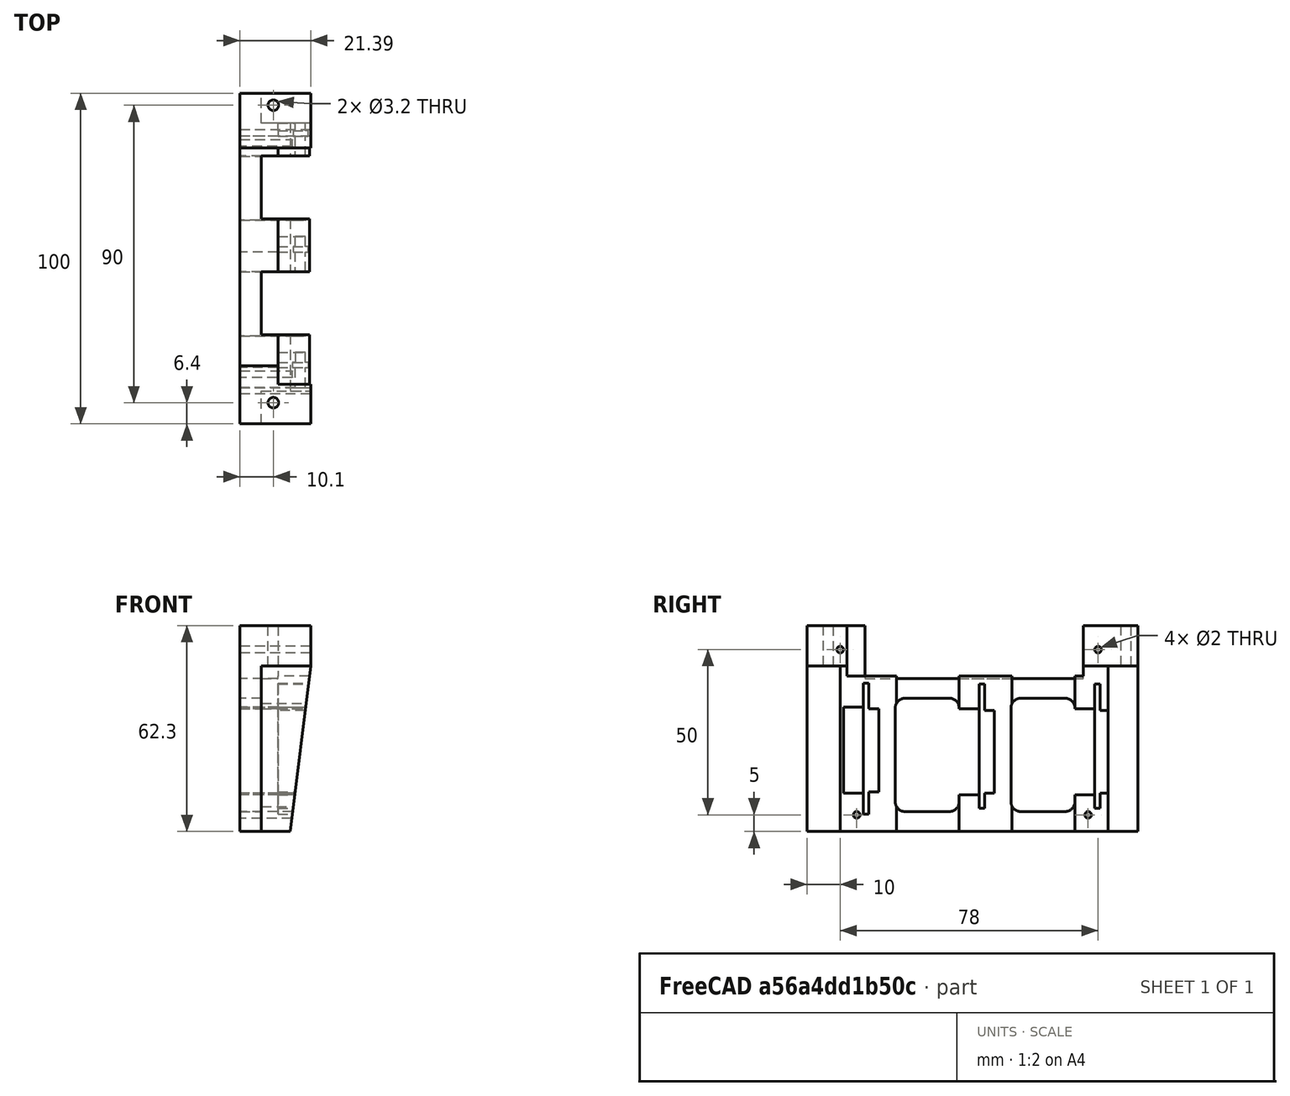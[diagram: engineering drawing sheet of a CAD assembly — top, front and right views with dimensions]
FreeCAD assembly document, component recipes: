
FREECAD ASSEMBLY — COMPONENT RECIPES ("sborka")

This assembly document has 10 components, labeled P0..P9 below (a component is one placed body or linked part). 7 of them carry a construction recipe — the FreeCAD feature program that regenerates the part from scratch, quoted from this document or its linked companion documents; the rest are supplied as boundary geometry only. No exploded tour is included for this assembly.
COMPONENT P0 — geometry summary ("keypad"; no construction recipe available for this part):
  bounding box: 75.0 x 69.0 x 2.0 mm
  tessellated surface: 12 triangles
  volume: 10350 mm^3 (100% of its bounding box)
  symmetry: 2-fold rotationally symmetric about the x axis; 2-fold rotationally symmetric about the y axis; 2-fold rotationally symmetric about the z axis; mirror-symmetric across its x mid-plane, z mid-plane
COMPONENT P1 — geometry summary ("3_97inch_LCD001"; no construction recipe available for this part):
  bounding box: 112.0 x 59.5 x 14.1 mm
  tessellated surface: 92 triangles
  volume: 35557 mm^3 (38% of its bounding box)
  symmetry: mirror-symmetric across its z mid-plane
COMPONENT P2 — recipe-attached ("acd_dac_board", a linked part whose construction recipe lives in a companion FreeCAD document of the same project; that document's serialized recipe follows).
Construction recipe (the companion document, serialized — sketch geometry with constraints, then the solid features built on it; lengths are millimeters unless a unit is written):

FCSTD DOCUMENT  (FreeCAD 1.0R39109 (Git))
Label: acd_dac_board
License: All rights reserved
LicenseURL: https://en.wikipedia.org/wiki/All_rights_reserved
objects: App::Part×6, App::Link×5, Part::Feature×4, PartDesign::CoordinateSystem×1, Sketcher::SketchObject×1
note: 7 computed .brp shape members not serialized (recipe doc carries the construction recipe); baked Part::Feature solids carry a one-line shape summary decoded from their .brp

FEATURE [PartDesign::CoordinateSystem] Local_CS_c5fe
  AttacherType = Attacher::AttachEngine3D
  MapMode = 2
FEATURE [Part::Feature] Pcb_c5fe
  shape: bbox 90 x 60 x 1.6 mm, 120 faces (baked)
FEATURE [Sketcher::SketchObject] PCB_Sketch_c5fe
  ArcFitTolerance = 1e-06
  FullyConstrained = false
  MakeInternals = false
  sketch-geometry (4):
    g0: LineSegment StartX=93.9 StartY=-71.9 StartZ=0 EndX=183.9 EndY=-71.9 EndZ=0
    g1: LineSegment StartX=183.9 StartY=-71.9 StartZ=0 EndX=183.9 EndY=-131.9 EndZ=0
    g2: LineSegment StartX=183.9 StartY=-131.9 StartZ=0 EndX=93.9 EndY=-131.9 EndZ=0
    g3: LineSegment StartX=93.9 StartY=-131.9 StartZ=0 EndX=93.9 EndY=-71.9 EndZ=0
  constraints (4):
    c: Coincident(g2,g3)
    c: Coincident(g0,g3)
    c: Coincident(g1,g2)
    c: Coincident(g0,g1)
FEATURE [App::Part] Board_Geoms_c5fe
  Group = -> [Pcb_c5fe,PCB_Sketch_c5fe]
  Origin = -> Origin
FEATURE [Part::Feature] Shape  label="J4_PinHeader_2x25_P254mm_Horizontal_27a54bd5aef3"
  Placement = pos=(168.5,-117.06,0) rot=(0,0,-1;1.5708rad)
  shape: bbox 63.5 x 12.9 x 8.08 mm, 1204 faces (baked)
FEATURE [Part::Feature] Shape001  label="J3_PinSocket_2x10_P2.54mm_Vertical_5a6bbbb15814"
  Placement = pos=(174.8,-83.06,0) rot=(0,0,1;0rad)
  shape: bbox 5.08 x 25.4 x 11.6 mm, 530 faces (baked)
FEATURE [App::Link] J3_PinSocket_2x10_P2_54mm_Vertical_5a6bbbb15814_ln_  label="J1_PinSocket_2x10_P2.54mm_Vertical_580dcfef748e"
  LinkPlacement = pos=(104.8,-83.06,0) rot=(0,0,1;0rad)
  LinkedObject = -> Shape001
  Placement = pos=(104.8,-83.06,0) rot=(0,0,1;0rad)
FEATURE [App::Link] J3_PinSocket_2x10_P2_54mm_Vertical_5a6bbbb15814_ln_001  label="J2_PinSocket_2x10_P2.54mm_Vertical_61ef51b03cdf"
  LinkPlacement = pos=(139.8,-83.06,0) rot=(0,0,1;0rad)
  LinkedObject = -> Shape001
  Placement = pos=(139.8,-83.06,0) rot=(0,0,1;0rad)
FEATURE [App::Part] Top_c5fe
  Group = -> [Shape,Shape001,J3_PinSocket_2x10_P2_54mm_Vertical_5a6bbbb15814_ln_,J3_PinSocket_2x10_P2_54mm_Vertical_5a6bbbb15814_ln_001]
  Origin = -> Origin003
FEATURE [App::Part] Step_Models_c5fe
  Group = -> [Top_c5fe]
  Origin = -> Origin002
FEATURE [Part::Feature] Shape002  label="REF_2.5 mmx7-Screw_fc498af58895"
  Placement = pos=(173,-75.1,-1.6) rot=(0,1,0;3.14159rad)
  shape: bbox 5 x 5 x 8.693 mm, 8 faces (baked)
FEATURE [App::Link] REF_2_5_mmx7_Screw_fc498af58895_ln_  label="REF_REF_2.5 mmx7-Screw_7bb2b2d65ce1"
  LinkPlacement = pos=(178,-125.1,-1.6) rot=(0,1,0;3.14159rad)
  LinkedObject = -> Shape002
  Placement = pos=(178,-125.1,-1.6) rot=(0,1,0;3.14159rad)
FEATURE [App::Link] REF_2_5_mmx7_Screw_fc498af58895_ln_001  label="REF_REF_2.5 mmx7-Screw_5b3bb718906a"
  LinkPlacement = pos=(99.9,-125.1,-1.6) rot=(0,1,0;3.14159rad)
  LinkedObject = -> Shape002
  Placement = pos=(99.9,-125.1,-1.6) rot=(0,1,0;3.14159rad)
FEATURE [App::Link] REF_2_5_mmx7_Screw_fc498af58895_ln_002  label="REF_REF_2.5 mmx7-Screw_1ec84486e3c5"
  LinkPlacement = pos=(103,-75.1,-1.6) rot=(0,1,0;3.14159rad)
  LinkedObject = -> Shape002
  Placement = pos=(103,-75.1,-1.6) rot=(0,1,0;3.14159rad)
FEATURE [App::Part] BotV_c5fe
  Group = -> [Shape002,REF_2_5_mmx7_Screw_fc498af58895_ln_,REF_2_5_mmx7_Screw_fc498af58895_ln_001,REF_2_5_mmx7_Screw_fc498af58895_ln_002]
  Origin = -> Origin007
FEATURE [App::Part] Step_Virtual_Models_c5fe
  Group = -> [BotV_c5fe]
  Origin = -> Origin005
FEATURE [App::Part] Board_c5fe  label="acd_dac_board"
  Group = -> [Local_CS_c5fe,Board_Geoms_c5fe,Step_Models_c5fe,Step_Virtual_Models_c5fe]
  Origin = -> Origin001
COMPONENT P3 — recipe-attached ("adc", a linked part whose construction recipe lives in a companion FreeCAD document of the same project; that document's serialized recipe follows).
Construction recipe (the companion document, serialized — sketch geometry with constraints, then the solid features built on it; lengths are millimeters unless a unit is written):

FCSTD DOCUMENT  (FreeCAD 1.0R39109 (Git))
Label: ADC
License: All rights reserved
LicenseURL: https://en.wikipedia.org/wiki/All_rights_reserved
objects: App::Link×34, Part::Feature×13, App::Part×4, PartDesign::CoordinateSystem×1, Sketcher::SketchObject×1
note: 16 computed .brp shape members not serialized (recipe doc carries the construction recipe); baked Part::Feature solids carry a one-line shape summary decoded from their .brp

FEATURE [PartDesign::CoordinateSystem] Local_CS_3770
  AttacherType = Attacher::AttachEngine3D
  MapMode = 2
FEATURE [Part::Feature] Pcb_3770
  Placement = pos=(-93.74,138.54,0) rot=(0,0,1;0rad)
  shape: bbox 37 x 54 x 1.6 mm, 39 faces (baked)
FEATURE [Sketcher::SketchObject] PCB_Sketch_3770
  ArcFitTolerance = 1e-06
  FullyConstrained = false
  MakeInternals = false
  sketch-geometry (4):
    g0: LineSegment StartX=-31.24 StartY=51.04 StartZ=0 EndX=5.76 EndY=51.04 EndZ=0
    g1: LineSegment StartX=5.76 StartY=51.04 StartZ=0 EndX=5.76 EndY=-2.96 EndZ=0
    g2: LineSegment StartX=5.76 StartY=-2.96 StartZ=0 EndX=-31.24 EndY=-2.96 EndZ=0
    g3: LineSegment StartX=-31.24 StartY=-2.96 StartZ=0 EndX=-31.24 EndY=51.04 EndZ=0
  constraints (4):
    c: Coincident(g2,g3)
    c: Coincident(g0,g3)
    c: Coincident(g1,g2)
    c: Coincident(g0,g1)
FEATURE [App::Part] Board_Geoms_3770
  Group = -> [Pcb_3770,PCB_Sketch_3770]
  Origin = -> Origin
FEATURE [Part::Feature] Shape  label="REF_R_1206_3216Metric_301ddd0c36ed"
  Placement = pos=(-5.34,45.84,0) rot=(0,0,1;0rad)
  shape: bbox 3.2 x 1.6 x 0.55 mm, 26 faces (baked)
FEATURE [App::Link] REF_R_1206_3216Metric_301ddd0c36ed_ln_  label="REF_REF_R_1206_3216Metric_70df84f1ae34"
  LinkPlacement = pos=(-22.84,41.94,0) rot=(0,0,1;1.5708rad)
  LinkedObject = -> Shape
  Placement = pos=(-22.84,41.94,0) rot=(0,0,1;1.5708rad)
FEATURE [App::Link] REF_R_1206_3216Metric_301ddd0c36ed_ln_001  label="REF_REF_R_1206_3216Metric_a6f854153131"
  LinkPlacement = pos=(1.16,14.24,0) rot=(0,0,1;0rad)
  LinkedObject = -> Shape
  Placement = pos=(1.16,14.24,0) rot=(0,0,1;0rad)
FEATURE [Part::Feature] Shape001  label="REF_C_1206_3216Metric_e221a3b84079"
  Placement = pos=(-9.14,29.34,0) rot=(0,0,1;0rad)
  shape: bbox 3.2 x 1.6 x 1.6 mm, 28 faces (baked)
FEATURE [App::Link] REF_R_1206_3216Metric_301ddd0c36ed_ln_002  label="REF_REF_R_1206_3216Metric_a0f92e46f677"
  LinkPlacement = pos=(-10.64,32.94,0) rot=(0,0,1;1.5708rad)
  LinkedObject = -> Shape
  Placement = pos=(-10.64,32.94,0) rot=(0,0,1;1.5708rad)
FEATURE [Part::Feature] Shape002  label="REF_CP_Elec_63x77_d1b758cef271"
  Placement = pos=(-26.34,25.34,0) rot=(0,0,1;0rad)
  shape: bbox 8.606 x 8.603 x 7.7 mm, 41 faces (baked)
FEATURE [App::Link] REF_R_1206_3216Metric_301ddd0c36ed_ln_003  label="REF_REF_R_1206_3216Metric_1b9d2568f397"
  LinkPlacement = pos=(-20.24,41.94,0) rot=(0,0,1;1.5708rad)
  LinkedObject = -> Shape
  Placement = pos=(-20.24,41.94,0) rot=(0,0,1;1.5708rad)
FEATURE [Part::Feature] Shape003  label="REF_SOIC-8-1EP_3.9x4.9mm_P1.27mm_EP2.29x3mm_4b1fed1f54c1"
  Placement = pos=(-11.94,38.14,0) rot=(0,0,1;3.14159rad)
  shape: bbox 6 x 4.9 x 1.55 mm, 152 faces (baked)
FEATURE [App::Link] REF_C_1206_3216Metric_e221a3b84079_ln_  label="REF_REF_C_1206_3216Metric_3e90dc9b15e9"
  LinkPlacement = pos=(-1.24,27.14,0) rot=(0,0,1;0rad)
  LinkedObject = -> Shape001
  Placement = pos=(-1.24,27.14,0) rot=(0,0,1;0rad)
FEATURE [App::Link] REF_C_1206_3216Metric_e221a3b84079_ln_001  label="REF_REF_C_1206_3216Metric_f21636db2d26"
  LinkPlacement = pos=(-7.14,24.54,0) rot=(0,0,1;0rad)
  LinkedObject = -> Shape001
  Placement = pos=(-7.14,24.54,0) rot=(0,0,1;0rad)
FEATURE [App::Link] REF_C_1206_3216Metric_e221a3b84079_ln_002  label="REF_REF_C_1206_3216Metric_18777c7b1951"
  LinkPlacement = pos=(-10.74,25.34,0) rot=(0,0,1;1.5708rad)
  LinkedObject = -> Shape001
  Placement = pos=(-10.74,25.34,0) rot=(0,0,1;1.5708rad)
FEATURE [App::Link] REF_R_1206_3216Metric_301ddd0c36ed_ln_004  label="REF_REF_R_1206_3216Metric_5a7a546a1d58"
  LinkPlacement = pos=(0.96,22.24,0) rot=(0,0,1;0rad)
  LinkedObject = -> Shape
  Placement = pos=(0.96,22.24,0) rot=(0,0,1;0rad)
FEATURE [App::Link] REF_R_1206_3216Metric_301ddd0c36ed_ln_005  label="REF_REF_R_1206_3216Metric_6cf90c486473"
  LinkPlacement = pos=(-18.04,8.54,0) rot=(0,0,1;1.5708rad)
  LinkedObject = -> Shape
  Placement = pos=(-18.04,8.54,0) rot=(0,0,1;1.5708rad)
FEATURE [Part::Feature] Shape004  label="REF_LED_1206_3216Metric_2fccf6a8874c"
  Placement = pos=(-21.24,30.24,0) rot=(0,0,1;1.5708rad)
  shape: bbox 1.6 x 3.2 x 1.1 mm, 50 faces (baked)
FEATURE [Part::Feature] Shape005  label="REF_PinHeader_1x02_P254mm_Vertical_da5b8ef0d3b1"
  Placement = pos=(-22.24,49.24,0) rot=(0,0,1;1.5708rad)
  shape: bbox 5.08 x 2.54 x 11.54 mm, 52 faces (baked)
FEATURE [App::Link] REF_C_1206_3216Metric_e221a3b84079_ln_003  label="REF_REF_C_1206_3216Metric_64c44e93813f"
  LinkPlacement = pos=(-16.44,19.84,0) rot=(0,0,1;1.5708rad)
  LinkedObject = -> Shape001
  Placement = pos=(-16.44,19.84,0) rot=(0,0,1;1.5708rad)
FEATURE [App::Link] REF_R_1206_3216Metric_301ddd0c36ed_ln_006  label="REF_REF_R_1206_3216Metric_3b6dfaf97a83"
  LinkPlacement = pos=(-5.34,48.74,0) rot=(0,0,1;0rad)
  LinkedObject = -> Shape
  Placement = pos=(-5.34,48.74,0) rot=(0,0,1;0rad)
FEATURE [App::Link] REF_R_1206_3216Metric_301ddd0c36ed_ln_007  label="REF_REF_R_1206_3216Metric_8c0fe4bfaf64"
  LinkPlacement = pos=(0.96,19.44,0) rot=(0,0,1;0rad)
  LinkedObject = -> Shape
  Placement = pos=(0.96,19.44,0) rot=(0,0,1;0rad)
FEATURE [App::Link] REF_C_1206_3216Metric_e221a3b84079_ln_004  label="REF_REF_C_1206_3216Metric_99c8eecee891"
  LinkPlacement = pos=(-13.14,25.34,0) rot=(0,0,1;1.5708rad)
  LinkedObject = -> Shape001
  Placement = pos=(-13.14,25.34,0) rot=(0,0,1;1.5708rad)
FEATURE [App::Link] REF_R_1206_3216Metric_301ddd0c36ed_ln_008  label="REF_REF_R_1206_3216Metric_75b0c98a4610"
  LinkPlacement = pos=(-6.34,35.04,0) rot=(0,0,1;1.5708rad)
  LinkedObject = -> Shape
  Placement = pos=(-6.34,35.04,0) rot=(0,0,1;1.5708rad)
FEATURE [App::Link] REF_C_1206_3216Metric_e221a3b84079_ln_005  label="REF_REF_C_1206_3216Metric_2542e80cc9ef"
  LinkPlacement = pos=(-4.74,29.34,0) rot=(0,0,1;0rad)
  LinkedObject = -> Shape001
  Placement = pos=(-4.74,29.34,0) rot=(0,0,1;0rad)
FEATURE [App::Link] REF_R_1206_3216Metric_301ddd0c36ed_ln_009  label="REF_REF_R_1206_3216Metric_7b8190f97f6e"
  LinkPlacement = pos=(-6.44,39.74,0) rot=(0,0,1;1.5708rad)
  LinkedObject = -> Shape
  Placement = pos=(-6.44,39.74,0) rot=(0,0,1;1.5708rad)
FEATURE [Part::Feature] Shape006  label="REF_R_Array_Concave_4x0603_6ebfddd59be7"
  Placement = pos=(-6.74,8.44,0) rot=(0,0,1;1.5708rad)
  shape: bbox 3.2 x 1.6 x 0.6 mm, 140 faces (baked)
FEATURE [App::Link] REF_C_1206_3216Metric_e221a3b84079_ln_006  label="REF_REF_C_1206_3216Metric_ddc78717e179"
  LinkPlacement = pos=(-2.54,20.84,0) rot=(0,0,1;1.5708rad)
  LinkedObject = -> Shape001
  Placement = pos=(-2.54,20.84,0) rot=(0,0,1;1.5708rad)
FEATURE [App::Link] REF_C_1206_3216Metric_e221a3b84079_ln_007  label="REF_REF_C_1206_3216Metric_0f9f458e9312"
  LinkPlacement = pos=(-26.64,39.44,0) rot=(0,0,1;0rad)
  LinkedObject = -> Shape001
  Placement = pos=(-26.64,39.44,0) rot=(0,0,1;0rad)
FEATURE [App::Link] REF_R_1206_3216Metric_301ddd0c36ed_ln_010  label="REF_REF_R_1206_3216Metric_e40d589cdbd9"
  LinkPlacement = pos=(1.06,17.04,0) rot=(0,0,1;0rad)
  LinkedObject = -> Shape
  Placement = pos=(1.06,17.04,0) rot=(0,0,1;0rad)
FEATURE [App::Link] REF_R_Array_Concave_4x0603_6ebfddd59be7_ln_  label="REF_REF_R_Array_Concave_4x0603_c1e9b6bea166"
  LinkPlacement = pos=(-10.74,8.44,0) rot=(0,0,1;1.5708rad)
  LinkedObject = -> Shape006
  Placement = pos=(-10.74,8.44,0) rot=(0,0,1;1.5708rad)
FEATURE [App::Link] REF_C_1206_3216Metric_e221a3b84079_ln_008  label="REF_REF_C_1206_3216Metric_0664d0335a5c"
  LinkPlacement = pos=(-2.54,15.14,0) rot=(0,0,1;1.5708rad)
  LinkedObject = -> Shape001
  Placement = pos=(-2.54,15.14,0) rot=(0,0,1;1.5708rad)
FEATURE [App::Link] REF_R_1206_3216Metric_301ddd0c36ed_ln_011  label="REF_REF_R_1206_3216Metric_d8d0c14688f2"
  LinkPlacement = pos=(-17.54,34.94,0) rot=(0,0,1;1.5708rad)
  LinkedObject = -> Shape
  Placement = pos=(-17.54,34.94,0) rot=(0,0,1;1.5708rad)
FEATURE [App::Link] REF_R_1206_3216Metric_301ddd0c36ed_ln_012  label="REF_REF_R_1206_3216Metric_336c34d7c97d"
  LinkPlacement = pos=(-3.84,8.34,0) rot=(0,0,1;1.5708rad)
  LinkedObject = -> Shape
  Placement = pos=(-3.84,8.34,0) rot=(0,0,1;1.5708rad)
FEATURE [Part::Feature] Shape007  label="REF_DG350-3.96-02P-12-00AH_5fb89e4e64b6"
  Placement = pos=(-23.64,20.84,0) rot=(0.57735,-0.57735,-0.57735;2.0944rad)
  shape: bbox 6.8 x 8 x 11.9 mm, 434 faces (baked)
FEATURE [App::Link] REF_C_1206_3216Metric_e221a3b84079_ln_009  label="REF_REF_C_1206_3216Metric_c52bb9b8716f"
  LinkPlacement = pos=(-3.64,39.84,0) rot=(0,0,1;1.5708rad)
  LinkedObject = -> Shape001
  Placement = pos=(-3.64,39.84,0) rot=(0,0,1;1.5708rad)
FEATURE [App::Link] REF_R_1206_3216Metric_301ddd0c36ed_ln_013  label="REF_REF_R_1206_3216Metric_975d7f625023"
  LinkPlacement = pos=(-17.14,25.54,0) rot=(0,0,1;1.5708rad)
  LinkedObject = -> Shape
  Placement = pos=(-17.14,25.54,0) rot=(0,0,1;1.5708rad)
FEATURE [App::Link] REF_C_1206_3216Metric_e221a3b84079_ln_010  label="REF_REF_C_1206_3216Metric_4ccb42aa522b"
  LinkPlacement = pos=(-7.14,26.84,0) rot=(0,0,1;0rad)
  LinkedObject = -> Shape001
  Placement = pos=(-7.14,26.84,0) rot=(0,0,1;0rad)
FEATURE [Part::Feature] Shape008  label="REF_SOT_223_e5314abddc11"
  Placement = pos=(-26.54,33.34,0) rot=(0,0,1;1.5708rad)
  shape: bbox 6.5 x 7 x 1.7 mm, 78 faces (baked)
FEATURE [Part::Feature] Shape009  label="REF_HJ-Tech-HJ-SMA175_5e94955ffa82"
  Placement = pos=(-9.14,49.04,0) rot=(0,0.707107,0.707107;3.14159rad)
  shape: bbox 8.673 x 18.44 x 9.575 mm, 56 faces (baked)
FEATURE [App::Link] REF_R_1206_3216Metric_301ddd0c36ed_ln_014  label="REF_REF_R_1206_3216Metric_01a2f680d26f"
  LinkPlacement = pos=(-21.44,34.74,0) rot=(0,0,1;1.5708rad)
  LinkedObject = -> Shape
  Placement = pos=(-21.44,34.74,0) rot=(0,0,1;1.5708rad)
FEATURE [Part::Feature] Shape010  label="REF_PinHeader_2x10_P254mm_Horizontal_88ad88291e13"
  Placement = pos=(-0.06,2.6,0) rot=(0,0,-1;1.5708rad)
  shape: bbox 25.4 x 12.9 x 8.08 mm, 484 faces (baked)
FEATURE [Part::Feature] Shape011  label="REF_LQFP_48_7x7mm_P05mm_d06fefb0920b"
  Placement = pos=(-9.84,17.34,0) rot=(0,0,1;0rad)
  shape: bbox 9 x 9 x 1.5 mm, 764 faces (baked)
FEATURE [App::Link] REF_R_1206_3216Metric_301ddd0c36ed_ln_015  label="REF_REF_R_1206_3216Metric_06fab732c749"
  LinkPlacement = pos=(-17.44,39.54,0) rot=(0,0,1;1.5708rad)
  LinkedObject = -> Shape
  Placement = pos=(-17.44,39.54,0) rot=(0,0,1;1.5708rad)
FEATURE [App::Link] REF_R_1206_3216Metric_301ddd0c36ed_ln_016  label="REF_REF_R_1206_3216Metric_0ba6753cf2ae"
  LinkPlacement = pos=(-5.44,43.24,0) rot=(0,0,1;0rad)
  LinkedObject = -> Shape
  Placement = pos=(-5.44,43.24,0) rot=(0,0,1;0rad)
FEATURE [App::Link] REF_R_1206_3216Metric_301ddd0c36ed_ln_017  label="REF_REF_R_1206_3216Metric_f8758bee8265"
  LinkPlacement = pos=(-13.04,32.94,0) rot=(0,0,1;1.5708rad)
  LinkedObject = -> Shape
  Placement = pos=(-13.04,32.94,0) rot=(0,0,1;1.5708rad)
FEATURE [App::Link] REF_R_Array_Concave_4x0603_6ebfddd59be7_ln_001  label="REF_REF_R_Array_Concave_4x0603_4768bc114470"
  LinkPlacement = pos=(-14.74,8.44,0) rot=(0,0,1;1.5708rad)
  LinkedObject = -> Shape006
  Placement = pos=(-14.74,8.44,0) rot=(0,0,1;1.5708rad)
FEATURE [App::Link] REF_C_1206_3216Metric_e221a3b84079_ln_011  label="REF_REF_C_1206_3216Metric_aac49cf074a5"
  LinkPlacement = pos=(-1.14,24.64,0) rot=(0,0,1;0rad)
  LinkedObject = -> Shape001
  Placement = pos=(-1.14,24.64,0) rot=(0,0,1;0rad)
FEATURE [App::Link] REF_C_1206_3216Metric_e221a3b84079_ln_012  label="REF_REF_C_1206_3216Metric_d76365948289"
  LinkPlacement = pos=(-3.74,35.04,0) rot=(0,0,1;1.5708rad)
  LinkedObject = -> Shape001
  Placement = pos=(-3.74,35.04,0) rot=(0,0,1;1.5708rad)
FEATURE [App::Link] REF_R_1206_3216Metric_301ddd0c36ed_ln_018  label="REF_REF_R_1206_3216Metric_e63bd7cbb3e0"
  LinkPlacement = pos=(-17.34,44.44,0) rot=(0,0,1;1.5708rad)
  LinkedObject = -> Shape
  Placement = pos=(-17.34,44.44,0) rot=(0,0,1;1.5708rad)
FEATURE [App::Part] Top_3770
  Group = -> [Shape,REF_R_1206_3216Metric_301ddd0c36ed_ln_,REF_R_1206_3216Metric_301ddd0c36ed_ln_001,Shape001,REF_R_1206_3216Metric_301ddd0c36ed_ln_002,Shape002,REF_R_1206_3216Metric_301ddd0c36ed_ln_003,Shape003,REF_C_1206_3216Metric_e221a3b84079_ln_,REF_C_1206_3216Metric_e221a3b84079_ln_001,REF_C_1206_3216Metric_e221a3b84079_ln_002,REF_R_1206_3216Metric_301ddd0c36ed_ln_004,+34 more]
  Origin = -> Origin003
FEATURE [App::Part] Step_Models_3770
  Group = -> [Top_3770]
  Origin = -> Origin002
FEATURE [App::Part] Board_3770  label="adc"
  Group = -> [Local_CS_3770,Board_Geoms_3770,Step_Models_3770]
  Origin = -> Origin001
COMPONENT P4 — same part as P3; its construction recipe is shown at P3.
COMPONENT P5 — recipe-attached ("dac", a linked part whose construction recipe lives in a companion FreeCAD document of the same project; that document's serialized recipe follows).
Construction recipe (the companion document, serialized — sketch geometry with constraints, then the solid features built on it; lengths are millimeters unless a unit is written):

FCSTD DOCUMENT  (FreeCAD 1.0R39109 (Git))
Label: dac
License: All rights reserved
LicenseURL: https://en.wikipedia.org/wiki/All_rights_reserved
objects: App::Link×47, Part::Feature×22, App::Part×10, PartDesign::CoordinateSystem×1, Sketcher::SketchObject×1
note: 25 computed .brp shape members not serialized (recipe doc carries the construction recipe); baked Part::Feature solids carry a one-line shape summary decoded from their .brp

FEATURE [PartDesign::CoordinateSystem] Local_CS_2375
  AttacherType = Attacher::AttachEngine3D
  MapMode = 2
FEATURE [Part::Feature] Pcb_2375
  Placement = pos=(-126.3,128.5,0) rot=(0,0,1;0rad)
  shape: bbox 39 x 56 x 1.6 mm, 70 faces (baked)
FEATURE [Sketcher::SketchObject] PCB_Sketch_2375
  ArcFitTolerance = 1e-06
  FullyConstrained = false
  MakeInternals = false
  sketch-geometry (4):
    g0: LineSegment StartX=-39 StartY=56 StartZ=0 EndX=0 EndY=56 EndZ=0
    g1: LineSegment StartX=0 StartY=56 StartZ=0 EndX=0 EndY=0 EndZ=0
    g2: LineSegment StartX=0 StartY=0 StartZ=0 EndX=-39 EndY=0 EndZ=0
    g3: LineSegment StartX=-39 StartY=0 StartZ=0 EndX=-39 EndY=56 EndZ=0
  constraints (4):
    c: Coincident(g2,g3)
    c: Coincident(g0,g3)
    c: Coincident(g1,g2)
    c: Coincident(g0,g1)
FEATURE [App::Part] Board_Geoms_2375
  Group = -> [Pcb_2375,PCB_Sketch_2375]
  Origin = -> Origin
FEATURE [Part::Feature] Shape  label="REF_TSSOP_28_44x97mm_P065mm_c3a42edb85d4"
  Placement = pos=(-16,18.3,0) rot=(0,0,1;1.5708rad)
  shape: bbox 9.7 x 6.4 x 1.1 mm, 456 faces (baked)
FEATURE [Part::Feature] Shape001  label="REF_R_1206_3216Metric_dea5eb461704"
  Placement = pos=(-13.3,41.1,0) rot=(0,0,1;1.5708rad)
  shape: bbox 1.6 x 3.2 x 0.55 mm, 26 faces (baked)
FEATURE [Part::Feature] Shape002  label="REF_L_1206_3216Metric_923911bd139e"
  Placement = pos=(-23.4,26.9,0) rot=(0,0,1;1.5708rad)
  shape: bbox 1.6 x 3.2 x 1.6 mm, 28 faces (baked)
FEATURE [Part::Feature] Shape003  label="REF_R_Array_Convex_4x0603_e66b4cefd16a"
  Placement = pos=(-18.3333,10.6,0) rot=(0,0,1;1.5708rad)
  shape: bbox 3.2 x 1.6 x 0.5 mm, 206 faces (baked)
FEATURE [Part::Feature] Shape004  label="REF_C_1812_4532Metric_fd35fdb9ec24"
  Placement = pos=(-34.9,37.2,0) rot=(0,0,1;0rad)
  shape: bbox 4.5 x 3.2 x 2.5 mm, 28 faces (baked)
FEATURE [Part::Feature] Shape005  label="REF_CP_Elec_63x77_0427d7c4acbc"
  Placement = pos=(-27.5,34.4,0) rot=(0,0,1;0rad)
  shape: bbox 8.606 x 8.603 x 7.7 mm, 41 faces (baked)
FEATURE [Part::Feature] Shape006  label="REF_D_SMA_bc62c40d3f1a"
  Placement = pos=(-35,30.6,0) rot=(0,0,1;0rad)
  shape: bbox 5 x 2.7 x 2.22 mm, 41 faces (baked)
FEATURE [App::Link] REF_R_Array_Convex_4x0603_e66b4cefd16a_ln_  label="REF_REF_R_Array_Convex_4x0603_60d2f3ed0a64"
  LinkPlacement = pos=(-14.1667,10.6,0) rot=(0,0,1;1.5708rad)
  LinkedObject = -> Shape003
  Placement = pos=(-14.1667,10.6,0) rot=(0,0,1;1.5708rad)
FEATURE [App::Link] REF_L_1206_3216Metric_923911bd139e_ln_  label="REF_REF_L_1206_3216Metric_92d995cbed52"
  LinkPlacement = pos=(-25.7,26.9,0) rot=(0,0,1;1.5708rad)
  LinkedObject = -> Shape002
  Placement = pos=(-25.7,26.9,0) rot=(0,0,1;1.5708rad)
FEATURE [Part::Feature] Shape007  label="REF_C_1206_3216Metric_ecc4e7f1350d"
  Placement = pos=(-25,21.6,0) rot=(0,0,1;3.14159rad)
  shape: bbox 3.2 x 1.6 x 1.6 mm, 28 faces (baked)
FEATURE [App::Link] REF_C_1206_3216Metric_ecc4e7f1350d_ln_  label="REF_REF_C_1206_3216Metric_d5ebf2718203"
  LinkPlacement = pos=(-9.4,26.9,0) rot=(0,0,1;1.5708rad)
  LinkedObject = -> Shape007
  Placement = pos=(-9.4,26.9,0) rot=(0,0,1;1.5708rad)
FEATURE [Part::Feature] Shape008  label="REF_PinHeader_2x10_P254mm_Horizontal_c3ac748f6938"
  Placement = pos=(-7.5,5.5,0) rot=(0,0,-1;1.5708rad)
  shape: bbox 25.4 x 12.9 x 8.08 mm, 484 faces (baked)
FEATURE [Part::Feature] Shape009  label="REF_PinHeader_1x02_P254mm_Vertical_c2c35adffc7d"
  Placement = pos=(-6.1,18,0) rot=(0,0,1;0rad)
  shape: bbox 2.54 x 5.08 x 11.54 mm, 52 faces (baked)
FEATURE [Part::Feature] Part__Feature  label="adbeea57-9c39-11ed-93f0-dde97e994e83_part"
  shape: bbox 2.5 x 4.5 x 1.5 mm, 12 faces (baked)
FEATURE [App::Part] adbeea57_9c39_11ed_93f0_dde97e994e83  label="adbeea57-9c39-11ed-93f0-dde97e994e83"
  Group = -> [Part__Feature]
  Origin = -> Origin008
FEATURE [Part::Feature] Part__Feature001  label="adbeea58-9c39-11ed-93f0-dde97e994e83_part"
  shape: bbox 2.5 x 1.6 x 0.4 mm, 12 faces (baked)
FEATURE [App::Part] adbeea58_9c39_11ed_93f0_dde97e994e83  label="adbeea58-9c39-11ed-93f0-dde97e994e83"
  Group = -> [Part__Feature001]
  Origin = -> Origin009
FEATURE [Part::Feature] Part__Feature002  label="adbeea59-9c39-11ed-93f0-dde97e994e83_part"
  shape: bbox 1.5 x 0.4 x 0.4 mm, 6 faces (baked)
FEATURE [Part::Feature] Part__Feature003  label="adbeea59-9c39-11ed-93f0-dde97e994e83_part001"
  shape: bbox 1.5 x 0.4 x 0.4 mm, 6 faces (baked)
FEATURE [Part::Feature] Part__Feature004  label="adbeea59-9c39-11ed-93f0-dde97e994e83_part002"
  shape: bbox 1.5 x 0.4 x 0.4 mm, 6 faces (baked)
FEATURE [App::Part] adbeea59_9c39_11ed_93f0_dde97e994e83_part  label="adbeea59-9c39-11ed-93f0-dde97e994e83_part003"
  Group = -> [Part__Feature002,Part__Feature003,Part__Feature004]
  Origin = -> Origin010
FEATURE [App::Part] adbeea59_9c39_11ed_93f0_dde97e994e83  label="adbeea59-9c39-11ed-93f0-dde97e994e83"
  Group = -> [adbeea59_9c39_11ed_93f0_dde97e994e83_part]
  Origin = -> Origin011
FEATURE [App::Part] adbeea56_9c39_11ed_93f0_dde97e994e83  label="adbeea56-9c39-11ed-93f0-dde97e994e83"
  Group = -> [adbeea57_9c39_11ed_93f0_dde97e994e83,adbeea58_9c39_11ed_93f0_dde97e994e83,adbeea59_9c39_11ed_93f0_dde97e994e83]
  Origin = -> Origin012
FEATURE [App::Part] CQ_assembly  label="REF_CQ assembly_e2316aff6ff6"
  Group = -> [adbeea56_9c39_11ed_93f0_dde97e994e83]
  Origin = -> Origin013
  Placement = pos=(-25.6,18.4,0) rot=(0,0,1;3.14159rad)
FEATURE [App::Link] REF_PinHeader_1x02_P254mm_Vertical_c2c35adffc7d_ln_  label="REF_REF_PinHeader_1x02_P254mm_Vertical_8d209ac5472d"
  LinkPlacement = pos=(-28,51.7,0) rot=(0,0,1;1.5708rad)
  LinkedObject = -> Shape009
  Placement = pos=(-28,51.7,0) rot=(0,0,1;1.5708rad)
FEATURE [App::Link] REF_R_1206_3216Metric_dea5eb461704_ln_  label="REF_REF_R_1206_3216Metric_28bc4882b059"
  LinkPlacement = pos=(-15.7,41.2,0) rot=(0,0,1;1.5708rad)
  LinkedObject = -> Shape001
  Placement = pos=(-15.7,41.2,0) rot=(0,0,1;1.5708rad)
FEATURE [App::Link] REF_C_1206_3216Metric_ecc4e7f1350d_ln_001  label="REF_REF_C_1206_3216Metric_9cc814834820"
  LinkPlacement = pos=(-18.7,26.9,0) rot=(0,0,1;1.5708rad)
  LinkedObject = -> Shape007
  Placement = pos=(-18.7,26.9,0) rot=(0,0,1;1.5708rad)
FEATURE [App::Link] REF_C_1206_3216Metric_ecc4e7f1350d_ln_002  label="REF_REF_C_1206_3216Metric_140ac1610760"
  LinkPlacement = pos=(-4.6,41.2,0) rot=(0,0,1;1.5708rad)
  LinkedObject = -> Shape007
  Placement = pos=(-4.6,41.2,0) rot=(0,0,1;1.5708rad)
FEATURE [Part::Feature] Shape010  label="REF_L_Cenker_CKCS4030_d8273a953477"
  Placement = pos=(-32,26,0) rot=(0,0,1;1.5708rad)
  shape: bbox 4 x 4.02 x 3 mm, 28 faces (baked)
FEATURE [App::Link] REF_C_1206_3216Metric_ecc4e7f1350d_ln_003  label="REF_REF_C_1206_3216Metric_1bdc9c04c953"
  LinkPlacement = pos=(-28.1,26.9,0) rot=(0,0,1;1.5708rad)
  LinkedObject = -> Shape007
  Placement = pos=(-28.1,26.9,0) rot=(0,0,1;1.5708rad)
FEATURE [App::Link] REF_C_1206_3216Metric_ecc4e7f1350d_ln_004  label="REF_REF_C_1206_3216Metric_cb06a00eb6bb"
  LinkPlacement = pos=(-14.1,26.9,0) rot=(0,0,1;1.5708rad)
  LinkedObject = -> Shape007
  Placement = pos=(-14.1,26.9,0) rot=(0,0,1;1.5708rad)
FEATURE [App::Link] REF_C_1206_3216Metric_ecc4e7f1350d_ln_005  label="REF_REF_C_1206_3216Metric_edc837841e0f"
  LinkPlacement = pos=(-14.5,36,0) rot=(0,0,1;1.5708rad)
  LinkedObject = -> Shape007
  Placement = pos=(-14.5,36,0) rot=(0,0,1;1.5708rad)
FEATURE [App::Link] REF_C_1206_3216Metric_ecc4e7f1350d_ln_006  label="REF_REF_C_1206_3216Metric_872d7316da85"
  LinkPlacement = pos=(-11.8,36,0) rot=(0,0,1;1.5708rad)
  LinkedObject = -> Shape007
  Placement = pos=(-11.8,36,0) rot=(0,0,1;1.5708rad)
FEATURE [App::Link] REF_C_1206_3216Metric_ecc4e7f1350d_ln_007  label="REF_REF_C_1206_3216Metric_fa080edd5de2"
  LinkPlacement = pos=(-34.7,33.7,0) rot=(0,0,1;3.14159rad)
  LinkedObject = -> Shape007
  Placement = pos=(-34.7,33.7,0) rot=(0,0,1;3.14159rad)
FEATURE [App::Link] REF_R_1206_3216Metric_dea5eb461704_ln_001  label="REF_REF_R_1206_3216Metric_daaedf7f6707"
  LinkPlacement = pos=(-7,26.9,0) rot=(0,0,1;1.5708rad)
  LinkedObject = -> Shape001
  Placement = pos=(-7,26.9,0) rot=(0,0,1;1.5708rad)
FEATURE [App::Link] REF_R_1206_3216Metric_dea5eb461704_ln_002  label="REF_REF_R_1206_3216Metric_e0c93ad1cb2a"
  LinkPlacement = pos=(-15.7,45.2,0) rot=(0,0,1;1.5708rad)
  LinkedObject = -> Shape001
  Placement = pos=(-15.7,45.2,0) rot=(0,0,1;1.5708rad)
FEATURE [Part::Feature] Shape011  label="REF_L_1210_3225Metric_5d334701bb60"
  Placement = pos=(-12.8,32.2,0) rot=(0,0,1;0rad)
  shape: bbox 3.2 x 2.5 x 2.5 mm, 28 faces (baked)
FEATURE [App::Link] REF_R_Array_Convex_4x0603_e66b4cefd16a_ln_001  label="REF_REF_R_Array_Convex_4x0603_f7815705a583"
  LinkPlacement = pos=(-22.5,10.6,0) rot=(0,0,1;1.5708rad)
  LinkedObject = -> Shape003
  Placement = pos=(-22.5,10.6,0) rot=(0,0,1;1.5708rad)
FEATURE [App::Link] REF_C_1206_3216Metric_ecc4e7f1350d_ln_008  label="REF_REF_C_1206_3216Metric_7a416d868406"
  LinkPlacement = pos=(-26.5,48.5,0) rot=(0,0,1;3.14159rad)
  LinkedObject = -> Shape007
  Placement = pos=(-26.5,48.5,0) rot=(0,0,1;3.14159rad)
FEATURE [App::Link] REF_L_1210_3225Metric_5d334701bb60_ln_  label="REF_REF_L_1210_3225Metric_272e2f4baf41"
  LinkPlacement = pos=(-17,32.2,0) rot=(0,0,1;0rad)
  LinkedObject = -> Shape011
  Placement = pos=(-17,32.2,0) rot=(0,0,1;0rad)
FEATURE [App::Link] REF_R_1206_3216Metric_dea5eb461704_ln_003  label="REF_REF_R_1206_3216Metric_4bb3a19c4e52"
  LinkPlacement = pos=(-22.1,36,0) rot=(0,0,1;1.5708rad)
  LinkedObject = -> Shape001
  Placement = pos=(-22.1,36,0) rot=(0,0,1;1.5708rad)
FEATURE [App::Link] REF_PinHeader_1x02_P254mm_Vertical_c2c35adffc7d_ln_001  label="REF_REF_PinHeader_1x02_P254mm_Vertical_c0119e070db1"
  LinkPlacement = pos=(-2.6,18,0) rot=(0,0,1;0rad)
  LinkedObject = -> Shape009
  Placement = pos=(-2.6,18,0) rot=(0,0,1;0rad)
FEATURE [Part::Feature] Shape012  label="REF_SOIC-8-1EP_3.9x4.9mm_P1.27mm_EP2.29x3mm_2a411558dc4c"
  Placement = pos=(-34.95,42.77,0) rot=(0,0,1;1.5708rad)
  shape: bbox 4.9 x 6 x 1.55 mm, 152 faces (baked)
FEATURE [App::Link] REF_L_1206_3216Metric_923911bd139e_ln_001  label="REF_REF_L_1206_3216Metric_39378e988feb"
  LinkPlacement = pos=(-21.2,26.9,0) rot=(0,0,1;1.5708rad)
  LinkedObject = -> Shape002
  Placement = pos=(-21.2,26.9,0) rot=(0,0,1;1.5708rad)
FEATURE [App::Link] REF_C_1812_4532Metric_fd35fdb9ec24_ln_  label="REF_REF_C_1812_4532Metric_d066acd0d603"
  LinkPlacement = pos=(-36.5,25.9,0) rot=(0,0,1;1.5708rad)
  LinkedObject = -> Shape004
  Placement = pos=(-36.5,25.9,0) rot=(0,0,1;1.5708rad)
FEATURE [App::Link] REF_L_1210_3225Metric_5d334701bb60_ln_001  label="REF_REF_L_1210_3225Metric_7fdfb9fc9615"
  LinkPlacement = pos=(-21.3,32.2,0) rot=(0,0,1;0rad)
  LinkedObject = -> Shape011
  Placement = pos=(-21.3,32.2,0) rot=(0,0,1;0rad)
FEATURE [App::Link] REF_R_1206_3216Metric_dea5eb461704_ln_004  label="REF_REF_R_1206_3216Metric_3d4d2a619084"
  LinkPlacement = pos=(-19,49.3,0) rot=(0,0,1;1.5708rad)
  LinkedObject = -> Shape001
  Placement = pos=(-19,49.3,0) rot=(0,0,1;1.5708rad)
FEATURE [App::Link] REF_C_1206_3216Metric_ecc4e7f1350d_ln_009  label="REF_REF_C_1206_3216Metric_46c0f67f32fe"
  LinkPlacement = pos=(-14.3,48.5,0) rot=(0,0,1;3.14159rad)
  LinkedObject = -> Shape007
  Placement = pos=(-14.3,48.5,0) rot=(0,0,1;3.14159rad)
FEATURE [App::Link] REF_R_1206_3216Metric_dea5eb461704_ln_005  label="REF_REF_R_1206_3216Metric_589fc75ea92f"
  LinkPlacement = pos=(-4.7,31.3,0) rot=(0,0,1;1.5708rad)
  LinkedObject = -> Shape001
  Placement = pos=(-4.7,31.3,0) rot=(0,0,1;1.5708rad)
FEATURE [App::Link] REF_SOIC_8_1EP_3_9x4_9mm_P1_27mm_EP2_29x3mm_2a411558dc4c_ln_  label="REF_REF_SOIC-8-1EP_3.9x4.9mm_P1.27mm_EP2.29x3mm_327c7d781933"
  LinkPlacement = pos=(-8.65,42.77,0) rot=(0,0,1;1.5708rad)
  LinkedObject = -> Shape012
  Placement = pos=(-8.65,42.77,0) rot=(0,0,1;1.5708rad)
FEATURE [App::Link] REF_R_1206_3216Metric_dea5eb461704_ln_006  label="REF_REF_R_1206_3216Metric_e1e13a756e31"
  LinkPlacement = pos=(-9.5,31.4,0) rot=(0,0,1;1.5708rad)
  LinkedObject = -> Shape001
  Placement = pos=(-9.5,31.4,0) rot=(0,0,1;1.5708rad)
FEATURE [App::Link] REF_C_1206_3216Metric_ecc4e7f1350d_ln_010  label="REF_REF_C_1206_3216Metric_d8d913f8484a"
  LinkPlacement = pos=(-11.8,26.9,0) rot=(0,0,1;1.5708rad)
  LinkedObject = -> Shape007
  Placement = pos=(-11.8,26.9,0) rot=(0,0,1;1.5708rad)
FEATURE [App::Link] REF_R_1206_3216Metric_dea5eb461704_ln_007  label="REF_REF_R_1206_3216Metric_857049673542"
  LinkPlacement = pos=(-4.6,36,0) rot=(0,0,1;1.5708rad)
  LinkedObject = -> Shape001
  Placement = pos=(-4.6,36,0) rot=(0,0,1;1.5708rad)
FEATURE [Part::Feature] Shape013  label="REF_LED_1206_3216Metric_d22cfbdbfb4d"
  Placement = pos=(-28.5,11.3,0) rot=(0,0,1;1.5708rad)
  shape: bbox 1.6 x 3.2 x 1.1 mm, 50 faces (baked)
FEATURE [App::Link] REF_C_1206_3216Metric_ecc4e7f1350d_ln_011  label="REF_REF_C_1206_3216Metric_7f81c6af838c"
  LinkPlacement = pos=(-19.6,36,0) rot=(0,0,1;1.5708rad)
  LinkedObject = -> Shape007
  Placement = pos=(-19.6,36,0) rot=(0,0,1;1.5708rad)
FEATURE [App::Link] REF_C_1206_3216Metric_ecc4e7f1350d_ln_012  label="REF_REF_C_1206_3216Metric_c4aa7e021370"
  LinkPlacement = pos=(-13.4,45.2,0) rot=(0,0,1;1.5708rad)
  LinkedObject = -> Shape007
  Placement = pos=(-13.4,45.2,0) rot=(0,0,1;1.5708rad)
FEATURE [App::Link] REF_C_1206_3216Metric_ecc4e7f1350d_ln_013  label="REF_REF_C_1206_3216Metric_57fe54d1a34d"
  LinkPlacement = pos=(-24.2,45.1,0) rot=(0,0,1;1.5708rad)
  LinkedObject = -> Shape007
  Placement = pos=(-24.2,45.1,0) rot=(0,0,1;1.5708rad)
FEATURE [Part::Feature] Shape014  label="REF_SMA_Samtec_SMA-J-P-H-ST-EM1_EdgeMount_10ab1944b6c5"
  Placement = pos=(-19.2,54.4375,0) rot=(0,0,1;1.5708rad)
  shape: bbox 6.633 x 13.33 x 6.523 mm, 69 faces (baked)
FEATURE [App::Link] REF_R_1206_3216Metric_dea5eb461704_ln_008  label="REF_REF_R_1206_3216Metric_5fd7c2efb940"
  LinkPlacement = pos=(-7,31.3,0) rot=(0,0,1;1.5708rad)
  LinkedObject = -> Shape001
  Placement = pos=(-7,31.3,0) rot=(0,0,1;1.5708rad)
FEATURE [App::Link] REF_R_1206_3216Metric_dea5eb461704_ln_009  label="REF_REF_R_1206_3216Metric_8f214b9c0e7f"
  LinkPlacement = pos=(-9.5,36,0) rot=(0,0,1;1.5708rad)
  LinkedObject = -> Shape001
  Placement = pos=(-9.5,36,0) rot=(0,0,1;1.5708rad)
FEATURE [App::Link] REF_C_1206_3216Metric_ecc4e7f1350d_ln_014  label="REF_REF_C_1206_3216Metric_6b1bf2e510a7"
  LinkPlacement = pos=(-22.4,48.5,0) rot=(0,0,1;3.14159rad)
  LinkedObject = -> Shape007
  Placement = pos=(-22.4,48.5,0) rot=(0,0,1;3.14159rad)
FEATURE [App::Link] REF_R_1206_3216Metric_dea5eb461704_ln_010  label="REF_REF_R_1206_3216Metric_47425226c818"
  LinkPlacement = pos=(-16.3,26.9,0) rot=(0,0,1;1.5708rad)
  LinkedObject = -> Shape001
  Placement = pos=(-16.3,26.9,0) rot=(0,0,1;1.5708rad)
FEATURE [App::Link] REF_R_1206_3216Metric_dea5eb461704_ln_011  label="REF_REF_R_1206_3216Metric_96f9e62eec0e"
  LinkPlacement = pos=(-7.1,36,0) rot=(0,0,1;1.5708rad)
  LinkedObject = -> Shape001
  Placement = pos=(-7.1,36,0) rot=(0,0,1;1.5708rad)
FEATURE [App::Link] REF_R_1206_3216Metric_dea5eb461704_ln_012  label="REF_REF_R_1206_3216Metric_56ab30c5af69"
  LinkPlacement = pos=(-25.8,11,0) rot=(0,0,1;1.5708rad)
  LinkedObject = -> Shape001
  Placement = pos=(-25.8,11,0) rot=(0,0,1;1.5708rad)
FEATURE [App::Link] REF_R_Array_Convex_4x0603_e66b4cefd16a_ln_002  label="REF_REF_R_Array_Convex_4x0603_f290d0503860"
  LinkPlacement = pos=(-10,10.6,0) rot=(0,0,1;1.5708rad)
  LinkedObject = -> Shape003
  Placement = pos=(-10,10.6,0) rot=(0,0,1;1.5708rad)
FEATURE [App::Link] REF_C_1206_3216Metric_ecc4e7f1350d_ln_015  label="REF_REF_C_1206_3216Metric_dc8951aa932c"
  LinkPlacement = pos=(-24.8,14.8,0) rot=(0,0,1;3.14159rad)
  LinkedObject = -> Shape007
  Placement = pos=(-24.8,14.8,0) rot=(0,0,1;3.14159rad)
FEATURE [Part::Feature] Shape015  label="REF_DG350-3.96-02P-12-00AH_d845d113af01"
  Placement = pos=(-31.7,20.8,0) rot=(0.57735,-0.57735,-0.57735;2.0944rad)
  shape: bbox 6.8 x 8 x 11.9 mm, 434 faces (baked)
FEATURE [App::Link] REF_R_1206_3216Metric_dea5eb461704_ln_013  label="REF_REF_R_1206_3216Metric_6aedbf5a6e43"
  LinkPlacement = pos=(-24.1,41.1,0) rot=(0,0,1;1.5708rad)
  LinkedObject = -> Shape001
  Placement = pos=(-24.1,41.1,0) rot=(0,0,1;1.5708rad)
FEATURE [App::Link] REF_R_1206_3216Metric_dea5eb461704_ln_014  label="REF_REF_R_1206_3216Metric_874934694a7d"
  LinkPlacement = pos=(-4.6,26.9,0) rot=(0,0,1;1.5708rad)
  LinkedObject = -> Shape001
  Placement = pos=(-4.6,26.9,0) rot=(0,0,1;1.5708rad)
FEATURE [App::Link] REF_R_1206_3216Metric_dea5eb461704_ln_015  label="REF_REF_R_1206_3216Metric_748cbaacc74b"
  LinkPlacement = pos=(-4.6,45.6,0) rot=(0,0,1;1.5708rad)
  LinkedObject = -> Shape001
  Placement = pos=(-4.6,45.6,0) rot=(0,0,1;1.5708rad)
FEATURE [App::Link] REF_C_1206_3216Metric_ecc4e7f1350d_ln_016  label="REF_REF_C_1206_3216Metric_436c53fa4e84"
  LinkPlacement = pos=(-17,36,0) rot=(0,0,1;1.5708rad)
  LinkedObject = -> Shape007
  Placement = pos=(-17,36,0) rot=(0,0,1;1.5708rad)
FEATURE [App::Link] REF_SOIC_8_1EP_3_9x4_9mm_P1_27mm_EP2_29x3mm_2a411558dc4c_ln_001  label="REF_REF_SOIC-8-1EP_3.9x4.9mm_P1.27mm_EP2.29x3mm_3479d8ad36aa"
  LinkPlacement = pos=(-20.05,42.77,0) rot=(0,0,1;1.5708rad)
  LinkedObject = -> Shape012
  Placement = pos=(-20.05,42.77,0) rot=(0,0,1;1.5708rad)
FEATURE [App::Link] REF_L_Cenker_CKCS4030_d8273a953477_ln_  label="REF_REF_L_Cenker_CKCS4030_3209fc811b72"
  LinkPlacement = pos=(-29,43.4,0) rot=(0,0,1;1.5708rad)
  LinkedObject = -> Shape010
  Placement = pos=(-29,43.4,0) rot=(0,0,1;1.5708rad)
FEATURE [App::Link] REF_C_1206_3216Metric_ecc4e7f1350d_ln_017  label="REF_REF_C_1206_3216Metric_a79974573d3d"
  LinkPlacement = pos=(-30.9,48.4,0) rot=(0,0,1;3.14159rad)
  LinkedObject = -> Shape007
  Placement = pos=(-30.9,48.4,0) rot=(0,0,1;3.14159rad)
FEATURE [App::Part] Top_2375
  Group = -> [Shape,Shape001,Shape002,Shape003,Shape004,Shape005,Shape006,REF_R_Array_Convex_4x0603_e66b4cefd16a_ln_,REF_L_1206_3216Metric_923911bd139e_ln_,Shape007,REF_C_1206_3216Metric_ecc4e7f1350d_ln_,Shape008,Shape009,CQ_assembly,REF_PinHeader_1x02_P254mm_Vertical_c2c35adffc7d_ln_,REF_R_1206_3216Metric_dea5eb461704_ln_,REF_C_1206_3216Metric_ecc4e7f1350d_ln_001,REF_C_1206_3216Metric_ecc4e7f1350d_ln_002,+46 more]
  Origin = -> Origin003
FEATURE [App::Part] Step_Models_2375
  Group = -> [Top_2375]
  Origin = -> Origin002
FEATURE [App::Part] Board_2375  label="dac"
  Group = -> [Local_CS_2375,Board_Geoms_2375,Step_Models_2375]
  Origin = -> Origin001
COMPONENT P6 — recipe-attached ("fpga", a linked part whose construction recipe lives in a companion FreeCAD document of the same project; that document's serialized recipe follows).
Construction recipe (the companion document, serialized — sketch geometry with constraints, then the solid features built on it; lengths are millimeters unless a unit is written):

FCSTD DOCUMENT  (FreeCAD 1.0R39109 (Git))
Label: fpga
License: All rights reserved
LicenseURL: https://en.wikipedia.org/wiki/All_rights_reserved
objects: Part::Feature×337, App::Link×33, App::Part×6, PartDesign::CoordinateSystem×1, Sketcher::SketchObject×1
note: 340 computed .brp shape members not serialized (recipe doc carries the construction recipe); baked Part::Feature solids carry a one-line shape summary decoded from their .brp

FEATURE [PartDesign::CoordinateSystem] Local_CS_4879
  AttacherType = Attacher::AttachEngine3D
  MapMode = 2
FEATURE [Part::Feature] Pcb_4879
  Placement = pos=(-72.6,67.6,0) rot=(0,0,1;0rad)
  shape: bbox 66.2 x 57 x 1.6 mm, 114 faces (baked)
FEATURE [Sketcher::SketchObject] PCB_Sketch_4879
  ArcFitTolerance = 1e-06
  FullyConstrained = false
  MakeInternals = false
  sketch-geometry (4):
    g0: LineSegment StartX=-2.6 StartY=1.81 StartZ=0 EndX=63.6 EndY=1.81 EndZ=0
    g1: LineSegment StartX=63.6 StartY=1.81 StartZ=0 EndX=63.6 EndY=-55.19 EndZ=0
    g2: LineSegment StartX=63.6 StartY=-55.19 StartZ=0 EndX=-2.6 EndY=-55.19 EndZ=0
    g3: LineSegment StartX=-2.6 StartY=-55.19 StartZ=0 EndX=-2.6 EndY=1.81 EndZ=0
  constraints (4):
    c: Coincident(g2,g3)
    c: Coincident(g0,g3)
    c: Coincident(g1,g2)
    c: Coincident(g0,g1)
FEATURE [App::Part] Board_Geoms_4879
  Group = -> [Pcb_4879,PCB_Sketch_4879]
  Origin = -> Origin
FEATURE [Part::Feature] Shape  label="REF_R_0603_1608Metric_0f1490cb362e"
  Placement = pos=(54.9,-43.6,0) rot=(0,0,1;1.5708rad)
  shape: bbox 0.8 x 1.6 x 0.45 mm, 26 faces (baked)
FEATURE [Part::Feature] Shape001  label="REF_C_1206_3216Metric_fe751edea67d"
  Placement = pos=(15.1,-17.9,0) rot=(0,0,1;0rad)
  shape: bbox 3.2 x 1.6 x 1.6 mm, 28 faces (baked)
FEATURE [App::Link] REF_R_0603_1608Metric_0f1490cb362e_ln_  label="REF_REF_R_0603_1608Metric_4086e2bf5a6f"
  LinkPlacement = pos=(5,-6.5,0) rot=(0,0,1;3.14159rad)
  LinkedObject = -> Shape
  Placement = pos=(5,-6.5,0) rot=(0,0,1;3.14159rad)
FEATURE [App::Link] REF_R_0603_1608Metric_0f1490cb362e_ln_001  label="REF_REF_R_0603_1608Metric_15f21322d367"
  LinkPlacement = pos=(4.525,-47.4,0) rot=(0,0,1;0rad)
  LinkedObject = -> Shape
  Placement = pos=(4.525,-47.4,0) rot=(0,0,1;0rad)
FEATURE [App::Link] REF_R_0603_1608Metric_0f1490cb362e_ln_002  label="REF_REF_R_0603_1608Metric_3c88d43f2406"
  LinkPlacement = pos=(51.875,-15.4,0) rot=(0,0,1;0rad)
  LinkedObject = -> Shape
  Placement = pos=(51.875,-15.4,0) rot=(0,0,1;0rad)
FEATURE [Part::Feature] Shape002  label="REF_C_0805_2012Metric_293c7b1e92e5"
  Placement = pos=(44.1,-21.2,0) rot=(0,0,1;0rad)
  shape: bbox 2 x 1.25 x 1.25 mm, 28 faces (baked)
FEATURE [App::Link] REF_C_0805_2012Metric_293c7b1e92e5_ln_  label="REF_REF_C_0805_2012Metric_e3600786c86c"
  LinkPlacement = pos=(43.7,-19.2,0) rot=(0,0,1;0rad)
  LinkedObject = -> Shape002
  Placement = pos=(43.7,-19.2,0) rot=(0,0,1;0rad)
FEATURE [App::Link] REF_R_0603_1608Metric_0f1490cb362e_ln_003  label="REF_REF_R_0603_1608Metric_855a550cbd89"
  LinkPlacement = pos=(42.3,-15.3,0) rot=(0,0,1;0.785398rad)
  LinkedObject = -> Shape
  Placement = pos=(42.3,-15.3,0) rot=(0,0,1;0.785398rad)
FEATURE [App::Link] REF_R_0603_1608Metric_0f1490cb362e_ln_004  label="REF_REF_R_0603_1608Metric_fd1bddb6377b"
  LinkPlacement = pos=(52,-43.6,0) rot=(0,0,1;1.5708rad)
  LinkedObject = -> Shape
  Placement = pos=(52,-43.6,0) rot=(0,0,1;1.5708rad)
FEATURE [Part::Feature] Shape003  label="REF_LED_0805_2012Metric_89f5d563d29e"
  Placement = pos=(1.5,-12.6,0) rot=(0,0,1;0rad)
  shape: bbox 2 x 1.25 x 1.1 mm, 50 faces (baked)
FEATURE [App::Link] REF_C_0805_2012Metric_293c7b1e92e5_ln_001  label="REF_REF_C_0805_2012Metric_c9e512f8d478"
  LinkPlacement = pos=(43.2,-40.6,0) rot=(0,0,1;0rad)
  LinkedObject = -> Shape002
  Placement = pos=(43.2,-40.6,0) rot=(0,0,1;0rad)
FEATURE [Part::Feature] Shape004  label="REF_L_1008_2520Metric_d4302c7d8c7a"
  Placement = pos=(6,-28.8,0) rot=(0,0,1;0rad)
  shape: bbox 2.5 x 2 x 1.2 mm, 28 faces (baked)
FEATURE [App::Link] REF_R_0603_1608Metric_0f1490cb362e_ln_005  label="REF_REF_R_0603_1608Metric_5bbfde6b5cf9"
  LinkPlacement = pos=(4.9,-9.7,0) rot=(0,0,1;3.14159rad)
  LinkedObject = -> Shape
  Placement = pos=(4.9,-9.7,0) rot=(0,0,1;3.14159rad)
FEATURE [App::Link] REF_R_0603_1608Metric_0f1490cb362e_ln_006  label="REF_REF_R_0603_1608Metric_5dd8bf2d52d4"
  LinkPlacement = pos=(51.9,-6.5,0) rot=(0,0,1;0rad)
  LinkedObject = -> Shape
  Placement = pos=(51.9,-6.5,0) rot=(0,0,1;0rad)
FEATURE [App::Link] REF_C_1206_3216Metric_fe751edea67d_ln_  label="REF_REF_C_1206_3216Metric_b666c12ef766"
  LinkPlacement = pos=(5.8,-32.2,0) rot=(0,0,1;0rad)
  LinkedObject = -> Shape001
  Placement = pos=(5.8,-32.2,0) rot=(0,0,1;0rad)
FEATURE [App::Link] REF_L_1008_2520Metric_d4302c7d8c7a_ln_  label="REF_REF_L_1008_2520Metric_70e2b93ed768"
  LinkPlacement = pos=(6.3,-19,0) rot=(0,0,1;0rad)
  LinkedObject = -> Shape004
  Placement = pos=(6.3,-19,0) rot=(0,0,1;0rad)
FEATURE [App::Link] REF_C_1206_3216Metric_fe751edea67d_ln_001  label="REF_REF_C_1206_3216Metric_012bf2a306b9"
  LinkPlacement = pos=(1.2,-22.8,0) rot=(0,0,1;0rad)
  LinkedObject = -> Shape001
  Placement = pos=(1.2,-22.8,0) rot=(0,0,1;0rad)
FEATURE [App::Link] REF_C_1206_3216Metric_fe751edea67d_ln_002  label="REF_REF_C_1206_3216Metric_d13c57a152f7"
  LinkPlacement = pos=(6.1,-22.3,0) rot=(0,0,1;0rad)
  LinkedObject = -> Shape001
  Placement = pos=(6.1,-22.3,0) rot=(0,0,1;0rad)
FEATURE [App::Link] REF_LED_0805_2012Metric_89f5d563d29e_ln_  label="REF_REF_LED_0805_2012Metric_8f0bd3617327"
  LinkPlacement = pos=(1,-47.3,0) rot=(0,0,1;0rad)
  LinkedObject = -> Shape003
  Placement = pos=(1,-47.3,0) rot=(0,0,1;0rad)
FEATURE [App::Link] REF_R_0603_1608Metric_0f1490cb362e_ln_007  label="REF_REF_R_0603_1608Metric_8aac75f89add"
  LinkPlacement = pos=(40,-13.1,0) rot=(0,0,1;0.785398rad)
  LinkedObject = -> Shape
  Placement = pos=(40,-13.1,0) rot=(0,0,1;0.785398rad)
FEATURE [App::Link] REF_R_0603_1608Metric_0f1490cb362e_ln_008  label="REF_REF_R_0603_1608Metric_b6e1bb2ede0c"
  LinkPlacement = pos=(5.1,-12.6,0) rot=(0,0,1;3.14159rad)
  LinkedObject = -> Shape
  Placement = pos=(5.1,-12.6,0) rot=(0,0,1;3.14159rad)
FEATURE [Part::Feature] Shape005  label="REF_TSOT_23_5_5b1d7019fdeb"
  Placement = pos=(2.1,-17.6,0) rot=(0,0,1;1.5708rad)
  shape: bbox 2.9 x 2.8 x 0.95 mm, 109 faces (baked)
FEATURE [Part::Feature] Shape006  label="REF_L_APV_ANR4026_ce752ed03100"
  Placement = pos=(13.4,-24.3,0) rot=(0,0,1;0rad)
  shape: bbox 4.02 x 4 x 2.6 mm, 28 faces (baked)
FEATURE [Part::Feature] Shape007  label="REF_TSOP_II_54_222x1016mm_P08mm_f7b131a52fba"
  Placement = pos=(52.7,-30,0) rot=(0,0,1;0rad)
  shape: bbox 11.66 x 22.2 x 1.6 mm, 846 faces (baked)
FEATURE [App::Link] REF_C_0805_2012Metric_293c7b1e92e5_ln_002  label="REF_REF_C_0805_2012Metric_524983f23a06"
  LinkPlacement = pos=(16,-29.8,0) rot=(0,0,1;1.5708rad)
  LinkedObject = -> Shape002
  Placement = pos=(16,-29.8,0) rot=(0,0,1;1.5708rad)
FEATURE [App::Link] REF_C_0805_2012Metric_293c7b1e92e5_ln_003  label="REF_REF_C_0805_2012Metric_9d753e519493"
  LinkPlacement = pos=(60.6,-24.6,0) rot=(0,0,1;1.5708rad)
  LinkedObject = -> Shape002
  Placement = pos=(60.6,-24.6,0) rot=(0,0,1;1.5708rad)
FEATURE [Part::Feature] Part__Feature  label="XC7A35T-L1CSG324I"
  shape: bbox 15 x 1.2 x 15 mm, 6 faces (baked)
FEATURE [Part::Feature] Part__Feature001  label="XC7A35T-L1CSG324I001"
  shape: bbox 0.45 x 0.45 x 0.45 mm, 3 faces (baked)
FEATURE [Part::Feature] Part__Feature002  label="XC7A35T-L1CSG324I002"
  shape: bbox 0.45 x 0.45 x 0.45 mm, 3 faces (baked)
FEATURE [Part::Feature] Part__Feature003  label="XC7A35T-L1CSG324I003"
  shape: bbox 0.45 x 0.45 x 0.45 mm, 3 faces (baked)
FEATURE [Part::Feature] Part__Feature004  label="XC7A35T-L1CSG324I004"
  shape: bbox 0.45 x 0.45 x 0.45 mm, 3 faces (baked)
FEATURE [Part::Feature] Part__Feature005  label="XC7A35T-L1CSG324I005"
  shape: bbox 0.45 x 0.45 x 0.45 mm, 3 faces (baked)
FEATURE [Part::Feature] Part__Feature006  label="XC7A35T-L1CSG324I006"
  shape: bbox 0.45 x 0.45 x 0.45 mm, 3 faces (baked)
FEATURE [Part::Feature] Part__Feature007  label="XC7A35T-L1CSG324I007"
  shape: bbox 0.45 x 0.45 x 0.45 mm, 3 faces (baked)
FEATURE [Part::Feature] Part__Feature008  label="XC7A35T-L1CSG324I008"
  shape: bbox 0.45 x 0.45 x 0.45 mm, 3 faces (baked)
FEATURE [Part::Feature] Part__Feature009  label="XC7A35T-L1CSG324I009"
  shape: bbox 0.45 x 0.45 x 0.45 mm, 3 faces (baked)
FEATURE [Part::Feature] Part__Feature010  label="XC7A35T-L1CSG324I010"
  shape: bbox 0.45 x 0.45 x 0.45 mm, 3 faces (baked)
FEATURE [Part::Feature] Part__Feature011  label="XC7A35T-L1CSG324I011"
  shape: bbox 0.45 x 0.45 x 0.45 mm, 3 faces (baked)
FEATURE [Part::Feature] Part__Feature012  label="XC7A35T-L1CSG324I012"
  shape: bbox 0.45 x 0.45 x 0.45 mm, 3 faces (baked)
FEATURE [Part::Feature] Part__Feature013  label="XC7A35T-L1CSG324I013"
  shape: bbox 0.45 x 0.45 x 0.45 mm, 3 faces (baked)
FEATURE [Part::Feature] Part__Feature014  label="XC7A35T-L1CSG324I014"
  shape: bbox 0.45 x 0.45 x 0.45 mm, 3 faces (baked)
FEATURE [Part::Feature] Part__Feature015  label="XC7A35T-L1CSG324I015"
  shape: bbox 0.45 x 0.45 x 0.45 mm, 3 faces (baked)
FEATURE [Part::Feature] Part__Feature016  label="XC7A35T-L1CSG324I016"
  shape: bbox 0.45 x 0.45 x 0.45 mm, 3 faces (baked)
FEATURE [Part::Feature] Part__Feature017  label="XC7A35T-L1CSG324I017"
  shape: bbox 0.45 x 0.45 x 0.45 mm, 3 faces (baked)
FEATURE [Part::Feature] Part__Feature018  label="XC7A35T-L1CSG324I018"
  shape: bbox 0.45 x 0.45 x 0.45 mm, 3 faces (baked)
FEATURE [Part::Feature] Part__Feature019  label="XC7A35T-L1CSG324I019"
  shape: bbox 0.45 x 0.45 x 0.45 mm, 3 faces (baked)
FEATURE [Part::Feature] Part__Feature020  label="XC7A35T-L1CSG324I020"
  shape: bbox 0.45 x 0.45 x 0.45 mm, 3 faces (baked)
FEATURE [Part::Feature] Part__Feature021  label="XC7A35T-L1CSG324I021"
  shape: bbox 0.45 x 0.45 x 0.45 mm, 3 faces (baked)
FEATURE [Part::Feature] Part__Feature022  label="XC7A35T-L1CSG324I022"
  shape: bbox 0.45 x 0.45 x 0.45 mm, 3 faces (baked)
FEATURE [Part::Feature] Part__Feature023  label="XC7A35T-L1CSG324I023"
  shape: bbox 0.45 x 0.45 x 0.45 mm, 3 faces (baked)
FEATURE [Part::Feature] Part__Feature024  label="XC7A35T-L1CSG324I024"
  shape: bbox 0.45 x 0.45 x 0.45 mm, 3 faces (baked)
FEATURE [Part::Feature] Part__Feature025  label="XC7A35T-L1CSG324I025"
  shape: bbox 0.45 x 0.45 x 0.45 mm, 3 faces (baked)
FEATURE [Part::Feature] Part__Feature026  label="XC7A35T-L1CSG324I026"
  shape: bbox 0.45 x 0.45 x 0.45 mm, 3 faces (baked)
FEATURE [Part::Feature] Part__Feature027  label="XC7A35T-L1CSG324I027"
  shape: bbox 0.45 x 0.45 x 0.45 mm, 3 faces (baked)
FEATURE [Part::Feature] Part__Feature028  label="XC7A35T-L1CSG324I028"
  shape: bbox 0.45 x 0.45 x 0.45 mm, 3 faces (baked)
FEATURE [Part::Feature] Part__Feature029  label="XC7A35T-L1CSG324I029"
  shape: bbox 0.45 x 0.45 x 0.45 mm, 3 faces (baked)
FEATURE [Part::Feature] Part__Feature030  label="XC7A35T-L1CSG324I030"
  shape: bbox 0.45 x 0.45 x 0.45 mm, 3 faces (baked)
FEATURE [Part::Feature] Part__Feature031  label="XC7A35T-L1CSG324I031"
  shape: bbox 0.45 x 0.45 x 0.45 mm, 3 faces (baked)
FEATURE [Part::Feature] Part__Feature032  label="XC7A35T-L1CSG324I032"
  shape: bbox 0.45 x 0.45 x 0.45 mm, 3 faces (baked)
FEATURE [Part::Feature] Part__Feature033  label="XC7A35T-L1CSG324I033"
  shape: bbox 0.45 x 0.45 x 0.45 mm, 3 faces (baked)
FEATURE [Part::Feature] Part__Feature034  label="XC7A35T-L1CSG324I034"
  shape: bbox 0.45 x 0.45 x 0.45 mm, 3 faces (baked)
FEATURE [Part::Feature] Part__Feature035  label="XC7A35T-L1CSG324I035"
  shape: bbox 0.45 x 0.45 x 0.45 mm, 3 faces (baked)
FEATURE [Part::Feature] Part__Feature036  label="XC7A35T-L1CSG324I036"
  shape: bbox 0.45 x 0.45 x 0.45 mm, 3 faces (baked)
FEATURE [Part::Feature] Part__Feature037  label="XC7A35T-L1CSG324I037"
  shape: bbox 0.45 x 0.45 x 0.45 mm, 3 faces (baked)
FEATURE [Part::Feature] Part__Feature038  label="XC7A35T-L1CSG324I038"
  shape: bbox 0.45 x 0.45 x 0.45 mm, 3 faces (baked)
FEATURE [Part::Feature] Part__Feature039  label="XC7A35T-L1CSG324I039"
  shape: bbox 0.45 x 0.45 x 0.45 mm, 3 faces (baked)
FEATURE [Part::Feature] Part__Feature040  label="XC7A35T-L1CSG324I040"
  shape: bbox 0.45 x 0.45 x 0.45 mm, 3 faces (baked)
FEATURE [Part::Feature] Part__Feature041  label="XC7A35T-L1CSG324I041"
  shape: bbox 0.45 x 0.45 x 0.45 mm, 3 faces (baked)
FEATURE [Part::Feature] Part__Feature042  label="XC7A35T-L1CSG324I042"
  shape: bbox 0.45 x 0.45 x 0.45 mm, 3 faces (baked)
FEATURE [Part::Feature] Part__Feature043  label="XC7A35T-L1CSG324I043"
  shape: bbox 0.45 x 0.45 x 0.45 mm, 3 faces (baked)
FEATURE [Part::Feature] Part__Feature044  label="XC7A35T-L1CSG324I044"
  shape: bbox 0.45 x 0.45 x 0.45 mm, 3 faces (baked)
FEATURE [Part::Feature] Part__Feature045  label="XC7A35T-L1CSG324I045"
  shape: bbox 0.45 x 0.45 x 0.45 mm, 3 faces (baked)
FEATURE [Part::Feature] Part__Feature046  label="XC7A35T-L1CSG324I046"
  shape: bbox 0.45 x 0.45 x 0.45 mm, 3 faces (baked)
FEATURE [Part::Feature] Part__Feature047  label="XC7A35T-L1CSG324I047"
  shape: bbox 0.45 x 0.45 x 0.45 mm, 3 faces (baked)
FEATURE [Part::Feature] Part__Feature048  label="XC7A35T-L1CSG324I048"
  shape: bbox 0.45 x 0.45 x 0.45 mm, 3 faces (baked)
FEATURE [Part::Feature] Part__Feature049  label="XC7A35T-L1CSG324I049"
  shape: bbox 0.45 x 0.45 x 0.45 mm, 3 faces (baked)
FEATURE [Part::Feature] Part__Feature050  label="XC7A35T-L1CSG324I050"
  shape: bbox 0.45 x 0.45 x 0.45 mm, 3 faces (baked)
FEATURE [Part::Feature] Part__Feature051  label="XC7A35T-L1CSG324I051"
  shape: bbox 0.45 x 0.45 x 0.45 mm, 3 faces (baked)
FEATURE [Part::Feature] Part__Feature052  label="XC7A35T-L1CSG324I052"
  shape: bbox 0.45 x 0.45 x 0.45 mm, 3 faces (baked)
FEATURE [Part::Feature] Part__Feature053  label="XC7A35T-L1CSG324I053"
  shape: bbox 0.45 x 0.45 x 0.45 mm, 3 faces (baked)
FEATURE [Part::Feature] Part__Feature054  label="XC7A35T-L1CSG324I054"
  shape: bbox 0.45 x 0.45 x 0.45 mm, 3 faces (baked)
FEATURE [Part::Feature] Part__Feature055  label="XC7A35T-L1CSG324I055"
  shape: bbox 0.45 x 0.45 x 0.45 mm, 3 faces (baked)
FEATURE [Part::Feature] Part__Feature056  label="XC7A35T-L1CSG324I056"
  shape: bbox 0.45 x 0.45 x 0.45 mm, 3 faces (baked)
FEATURE [Part::Feature] Part__Feature057  label="XC7A35T-L1CSG324I057"
  shape: bbox 0.45 x 0.45 x 0.45 mm, 3 faces (baked)
FEATURE [Part::Feature] Part__Feature058  label="XC7A35T-L1CSG324I058"
  shape: bbox 0.45 x 0.45 x 0.45 mm, 3 faces (baked)
FEATURE [Part::Feature] Part__Feature059  label="XC7A35T-L1CSG324I059"
  shape: bbox 0.45 x 0.45 x 0.45 mm, 3 faces (baked)
FEATURE [Part::Feature] Part__Feature060  label="XC7A35T-L1CSG324I060"
  shape: bbox 0.45 x 0.45 x 0.45 mm, 3 faces (baked)
FEATURE [Part::Feature] Part__Feature061  label="XC7A35T-L1CSG324I061"
  shape: bbox 0.45 x 0.45 x 0.45 mm, 3 faces (baked)
FEATURE [Part::Feature] Part__Feature062  label="XC7A35T-L1CSG324I062"
  shape: bbox 0.45 x 0.45 x 0.45 mm, 3 faces (baked)
FEATURE [Part::Feature] Part__Feature063  label="XC7A35T-L1CSG324I063"
  shape: bbox 0.45 x 0.45 x 0.45 mm, 3 faces (baked)
FEATURE [Part::Feature] Part__Feature064  label="XC7A35T-L1CSG324I064"
  shape: bbox 0.45 x 0.45 x 0.45 mm, 3 faces (baked)
FEATURE [Part::Feature] Part__Feature065  label="XC7A35T-L1CSG324I065"
  shape: bbox 0.45 x 0.45 x 0.45 mm, 3 faces (baked)
FEATURE [Part::Feature] Part__Feature066  label="XC7A35T-L1CSG324I066"
  shape: bbox 0.45 x 0.45 x 0.45 mm, 3 faces (baked)
FEATURE [Part::Feature] Part__Feature067  label="XC7A35T-L1CSG324I067"
  shape: bbox 0.45 x 0.45 x 0.45 mm, 3 faces (baked)
FEATURE [Part::Feature] Part__Feature068  label="XC7A35T-L1CSG324I068"
  shape: bbox 0.45 x 0.45 x 0.45 mm, 3 faces (baked)
FEATURE [Part::Feature] Part__Feature069  label="XC7A35T-L1CSG324I069"
  shape: bbox 0.45 x 0.45 x 0.45 mm, 3 faces (baked)
FEATURE [Part::Feature] Part__Feature070  label="XC7A35T-L1CSG324I070"
  shape: bbox 0.45 x 0.45 x 0.45 mm, 3 faces (baked)
FEATURE [Part::Feature] Part__Feature071  label="XC7A35T-L1CSG324I071"
  shape: bbox 0.45 x 0.45 x 0.45 mm, 3 faces (baked)
FEATURE [Part::Feature] Part__Feature072  label="XC7A35T-L1CSG324I072"
  shape: bbox 0.45 x 0.45 x 0.45 mm, 3 faces (baked)
FEATURE [Part::Feature] Part__Feature073  label="XC7A35T-L1CSG324I073"
  shape: bbox 0.45 x 0.45 x 0.45 mm, 3 faces (baked)
FEATURE [Part::Feature] Part__Feature074  label="XC7A35T-L1CSG324I074"
  shape: bbox 0.45 x 0.45 x 0.45 mm, 3 faces (baked)
FEATURE [Part::Feature] Part__Feature075  label="XC7A35T-L1CSG324I075"
  shape: bbox 0.45 x 0.45 x 0.45 mm, 3 faces (baked)
FEATURE [Part::Feature] Part__Feature076  label="XC7A35T-L1CSG324I076"
  shape: bbox 0.45 x 0.45 x 0.45 mm, 3 faces (baked)
FEATURE [Part::Feature] Part__Feature077  label="XC7A35T-L1CSG324I077"
  shape: bbox 0.45 x 0.45 x 0.45 mm, 3 faces (baked)
FEATURE [Part::Feature] Part__Feature078  label="XC7A35T-L1CSG324I078"
  shape: bbox 0.45 x 0.45 x 0.45 mm, 3 faces (baked)
FEATURE [Part::Feature] Part__Feature079  label="XC7A35T-L1CSG324I079"
  shape: bbox 0.45 x 0.45 x 0.45 mm, 3 faces (baked)
FEATURE [Part::Feature] Part__Feature080  label="XC7A35T-L1CSG324I080"
  shape: bbox 0.45 x 0.45 x 0.45 mm, 3 faces (baked)
FEATURE [Part::Feature] Part__Feature081  label="XC7A35T-L1CSG324I081"
  shape: bbox 0.45 x 0.45 x 0.45 mm, 3 faces (baked)
FEATURE [Part::Feature] Part__Feature082  label="XC7A35T-L1CSG324I082"
  shape: bbox 0.45 x 0.45 x 0.45 mm, 3 faces (baked)
FEATURE [Part::Feature] Part__Feature083  label="XC7A35T-L1CSG324I083"
  shape: bbox 0.45 x 0.45 x 0.45 mm, 3 faces (baked)
FEATURE [Part::Feature] Part__Feature084  label="XC7A35T-L1CSG324I084"
  shape: bbox 0.45 x 0.45 x 0.45 mm, 3 faces (baked)
FEATURE [Part::Feature] Part__Feature085  label="XC7A35T-L1CSG324I085"
  shape: bbox 0.45 x 0.45 x 0.45 mm, 3 faces (baked)
FEATURE [Part::Feature] Part__Feature086  label="XC7A35T-L1CSG324I086"
  shape: bbox 0.45 x 0.45 x 0.45 mm, 3 faces (baked)
FEATURE [Part::Feature] Part__Feature087  label="XC7A35T-L1CSG324I087"
  shape: bbox 0.45 x 0.45 x 0.45 mm, 3 faces (baked)
FEATURE [Part::Feature] Part__Feature088  label="XC7A35T-L1CSG324I088"
  shape: bbox 0.45 x 0.45 x 0.45 mm, 3 faces (baked)
FEATURE [Part::Feature] Part__Feature089  label="XC7A35T-L1CSG324I089"
  shape: bbox 0.45 x 0.45 x 0.45 mm, 3 faces (baked)
FEATURE [Part::Feature] Part__Feature090  label="XC7A35T-L1CSG324I090"
  shape: bbox 0.45 x 0.45 x 0.45 mm, 3 faces (baked)
FEATURE [Part::Feature] Part__Feature091  label="XC7A35T-L1CSG324I091"
  shape: bbox 0.45 x 0.45 x 0.45 mm, 3 faces (baked)
FEATURE [Part::Feature] Part__Feature092  label="XC7A35T-L1CSG324I092"
  shape: bbox 0.45 x 0.45 x 0.45 mm, 3 faces (baked)
FEATURE [Part::Feature] Part__Feature093  label="XC7A35T-L1CSG324I093"
  shape: bbox 0.45 x 0.45 x 0.45 mm, 3 faces (baked)
FEATURE [Part::Feature] Part__Feature094  label="XC7A35T-L1CSG324I094"
  shape: bbox 0.45 x 0.45 x 0.45 mm, 3 faces (baked)
FEATURE [Part::Feature] Part__Feature095  label="XC7A35T-L1CSG324I095"
  shape: bbox 0.45 x 0.45 x 0.45 mm, 3 faces (baked)
FEATURE [Part::Feature] Part__Feature096  label="XC7A35T-L1CSG324I096"
  shape: bbox 0.45 x 0.45 x 0.45 mm, 3 faces (baked)
FEATURE [Part::Feature] Part__Feature097  label="XC7A35T-L1CSG324I097"
  shape: bbox 0.45 x 0.45 x 0.45 mm, 3 faces (baked)
FEATURE [Part::Feature] Part__Feature098  label="XC7A35T-L1CSG324I098"
  shape: bbox 0.45 x 0.45 x 0.45 mm, 3 faces (baked)
FEATURE [Part::Feature] Part__Feature099  label="XC7A35T-L1CSG324I099"
  shape: bbox 0.45 x 0.45 x 0.45 mm, 3 faces (baked)
FEATURE [Part::Feature] Part__Feature100  label="XC7A35T-L1CSG324I100"
  shape: bbox 0.45 x 0.45 x 0.45 mm, 3 faces (baked)
FEATURE [Part::Feature] Part__Feature101  label="XC7A35T-L1CSG324I101"
  shape: bbox 0.45 x 0.45 x 0.45 mm, 3 faces (baked)
FEATURE [Part::Feature] Part__Feature102  label="XC7A35T-L1CSG324I102"
  shape: bbox 0.45 x 0.45 x 0.45 mm, 3 faces (baked)
FEATURE [Part::Feature] Part__Feature103  label="XC7A35T-L1CSG324I103"
  shape: bbox 0.45 x 0.45 x 0.45 mm, 3 faces (baked)
FEATURE [Part::Feature] Part__Feature104  label="XC7A35T-L1CSG324I104"
  shape: bbox 0.45 x 0.45 x 0.45 mm, 3 faces (baked)
FEATURE [Part::Feature] Part__Feature105  label="XC7A35T-L1CSG324I105"
  shape: bbox 0.45 x 0.45 x 0.45 mm, 3 faces (baked)
FEATURE [Part::Feature] Part__Feature106  label="XC7A35T-L1CSG324I106"
  shape: bbox 0.45 x 0.45 x 0.45 mm, 3 faces (baked)
FEATURE [Part::Feature] Part__Feature107  label="XC7A35T-L1CSG324I107"
  shape: bbox 0.45 x 0.45 x 0.45 mm, 3 faces (baked)
FEATURE [Part::Feature] Part__Feature108  label="XC7A35T-L1CSG324I108"
  shape: bbox 0.45 x 0.45 x 0.45 mm, 3 faces (baked)
FEATURE [Part::Feature] Part__Feature109  label="XC7A35T-L1CSG324I109"
  shape: bbox 0.45 x 0.45 x 0.45 mm, 3 faces (baked)
FEATURE [Part::Feature] Part__Feature110  label="XC7A35T-L1CSG324I110"
  shape: bbox 0.45 x 0.45 x 0.45 mm, 3 faces (baked)
FEATURE [Part::Feature] Part__Feature111  label="XC7A35T-L1CSG324I111"
  shape: bbox 0.45 x 0.45 x 0.45 mm, 3 faces (baked)
FEATURE [Part::Feature] Part__Feature112  label="XC7A35T-L1CSG324I112"
  shape: bbox 0.45 x 0.45 x 0.45 mm, 3 faces (baked)
FEATURE [Part::Feature] Part__Feature113  label="XC7A35T-L1CSG324I113"
  shape: bbox 0.45 x 0.45 x 0.45 mm, 3 faces (baked)
FEATURE [Part::Feature] Part__Feature114  label="XC7A35T-L1CSG324I114"
  shape: bbox 0.45 x 0.45 x 0.45 mm, 3 faces (baked)
FEATURE [Part::Feature] Part__Feature115  label="XC7A35T-L1CSG324I115"
  shape: bbox 0.45 x 0.45 x 0.45 mm, 3 faces (baked)
FEATURE [Part::Feature] Part__Feature116  label="XC7A35T-L1CSG324I116"
  shape: bbox 0.45 x 0.45 x 0.45 mm, 3 faces (baked)
FEATURE [Part::Feature] Part__Feature117  label="XC7A35T-L1CSG324I117"
  shape: bbox 0.45 x 0.45 x 0.45 mm, 3 faces (baked)
FEATURE [Part::Feature] Part__Feature118  label="XC7A35T-L1CSG324I118"
  shape: bbox 0.45 x 0.45 x 0.45 mm, 3 faces (baked)
FEATURE [Part::Feature] Part__Feature119  label="XC7A35T-L1CSG324I119"
  shape: bbox 0.45 x 0.45 x 0.45 mm, 3 faces (baked)
FEATURE [Part::Feature] Part__Feature120  label="XC7A35T-L1CSG324I120"
  shape: bbox 0.45 x 0.45 x 0.45 mm, 3 faces (baked)
FEATURE [Part::Feature] Part__Feature121  label="XC7A35T-L1CSG324I121"
  shape: bbox 0.45 x 0.45 x 0.45 mm, 3 faces (baked)
FEATURE [Part::Feature] Part__Feature122  label="XC7A35T-L1CSG324I122"
  shape: bbox 0.45 x 0.45 x 0.45 mm, 3 faces (baked)
FEATURE [Part::Feature] Part__Feature123  label="XC7A35T-L1CSG324I123"
  shape: bbox 0.45 x 0.45 x 0.45 mm, 3 faces (baked)
FEATURE [Part::Feature] Part__Feature124  label="XC7A35T-L1CSG324I124"
  shape: bbox 0.45 x 0.45 x 0.45 mm, 3 faces (baked)
FEATURE [Part::Feature] Part__Feature125  label="XC7A35T-L1CSG324I125"
  shape: bbox 0.45 x 0.45 x 0.45 mm, 3 faces (baked)
FEATURE [Part::Feature] Part__Feature126  label="XC7A35T-L1CSG324I126"
  shape: bbox 0.45 x 0.45 x 0.45 mm, 3 faces (baked)
FEATURE [Part::Feature] Part__Feature127  label="XC7A35T-L1CSG324I127"
  shape: bbox 0.45 x 0.45 x 0.45 mm, 3 faces (baked)
FEATURE [Part::Feature] Part__Feature128  label="XC7A35T-L1CSG324I128"
  shape: bbox 0.45 x 0.45 x 0.45 mm, 3 faces (baked)
FEATURE [Part::Feature] Part__Feature129  label="XC7A35T-L1CSG324I129"
  shape: bbox 0.45 x 0.45 x 0.45 mm, 3 faces (baked)
FEATURE [Part::Feature] Part__Feature130  label="XC7A35T-L1CSG324I130"
  shape: bbox 0.45 x 0.45 x 0.45 mm, 3 faces (baked)
FEATURE [Part::Feature] Part__Feature131  label="XC7A35T-L1CSG324I131"
  shape: bbox 0.45 x 0.45 x 0.45 mm, 3 faces (baked)
FEATURE [Part::Feature] Part__Feature132  label="XC7A35T-L1CSG324I132"
  shape: bbox 0.45 x 0.45 x 0.45 mm, 3 faces (baked)
FEATURE [Part::Feature] Part__Feature133  label="XC7A35T-L1CSG324I133"
  shape: bbox 0.45 x 0.45 x 0.45 mm, 3 faces (baked)
FEATURE [Part::Feature] Part__Feature134  label="XC7A35T-L1CSG324I134"
  shape: bbox 0.45 x 0.45 x 0.45 mm, 3 faces (baked)
FEATURE [Part::Feature] Part__Feature135  label="XC7A35T-L1CSG324I135"
  shape: bbox 0.45 x 0.45 x 0.45 mm, 3 faces (baked)
FEATURE [Part::Feature] Part__Feature136  label="XC7A35T-L1CSG324I136"
  shape: bbox 0.45 x 0.45 x 0.45 mm, 3 faces (baked)
FEATURE [Part::Feature] Part__Feature137  label="XC7A35T-L1CSG324I137"
  shape: bbox 0.45 x 0.45 x 0.45 mm, 3 faces (baked)
FEATURE [Part::Feature] Part__Feature138  label="XC7A35T-L1CSG324I138"
  shape: bbox 0.45 x 0.45 x 0.45 mm, 3 faces (baked)
FEATURE [Part::Feature] Part__Feature139  label="XC7A35T-L1CSG324I139"
  shape: bbox 0.45 x 0.45 x 0.45 mm, 3 faces (baked)
FEATURE [Part::Feature] Part__Feature140  label="XC7A35T-L1CSG324I140"
  shape: bbox 0.45 x 0.45 x 0.45 mm, 3 faces (baked)
FEATURE [Part::Feature] Part__Feature141  label="XC7A35T-L1CSG324I141"
  shape: bbox 0.45 x 0.45 x 0.45 mm, 3 faces (baked)
FEATURE [Part::Feature] Part__Feature142  label="XC7A35T-L1CSG324I142"
  shape: bbox 0.45 x 0.45 x 0.45 mm, 3 faces (baked)
FEATURE [Part::Feature] Part__Feature143  label="XC7A35T-L1CSG324I143"
  shape: bbox 0.45 x 0.45 x 0.45 mm, 3 faces (baked)
FEATURE [Part::Feature] Part__Feature144  label="XC7A35T-L1CSG324I144"
  shape: bbox 0.45 x 0.45 x 0.45 mm, 3 faces (baked)
FEATURE [Part::Feature] Part__Feature145  label="XC7A35T-L1CSG324I145"
  shape: bbox 0.45 x 0.45 x 0.45 mm, 3 faces (baked)
FEATURE [Part::Feature] Part__Feature146  label="XC7A35T-L1CSG324I146"
  shape: bbox 0.45 x 0.45 x 0.45 mm, 3 faces (baked)
FEATURE [Part::Feature] Part__Feature147  label="XC7A35T-L1CSG324I147"
  shape: bbox 0.45 x 0.45 x 0.45 mm, 3 faces (baked)
FEATURE [Part::Feature] Part__Feature148  label="XC7A35T-L1CSG324I148"
  shape: bbox 0.45 x 0.45 x 0.45 mm, 3 faces (baked)
FEATURE [Part::Feature] Part__Feature149  label="XC7A35T-L1CSG324I149"
  shape: bbox 0.45 x 0.45 x 0.45 mm, 3 faces (baked)
FEATURE [Part::Feature] Part__Feature150  label="XC7A35T-L1CSG324I150"
  shape: bbox 0.45 x 0.45 x 0.45 mm, 3 faces (baked)
FEATURE [Part::Feature] Part__Feature151  label="XC7A35T-L1CSG324I151"
  shape: bbox 0.45 x 0.45 x 0.45 mm, 3 faces (baked)
FEATURE [Part::Feature] Part__Feature152  label="XC7A35T-L1CSG324I152"
  shape: bbox 0.45 x 0.45 x 0.45 mm, 3 faces (baked)
FEATURE [Part::Feature] Part__Feature153  label="XC7A35T-L1CSG324I153"
  shape: bbox 0.45 x 0.45 x 0.45 mm, 3 faces (baked)
FEATURE [Part::Feature] Part__Feature154  label="XC7A35T-L1CSG324I154"
  shape: bbox 0.45 x 0.45 x 0.45 mm, 3 faces (baked)
FEATURE [Part::Feature] Part__Feature155  label="XC7A35T-L1CSG324I155"
  shape: bbox 0.45 x 0.45 x 0.45 mm, 3 faces (baked)
FEATURE [Part::Feature] Part__Feature156  label="XC7A35T-L1CSG324I156"
  shape: bbox 0.45 x 0.45 x 0.45 mm, 3 faces (baked)
FEATURE [Part::Feature] Part__Feature157  label="XC7A35T-L1CSG324I157"
  shape: bbox 0.45 x 0.45 x 0.45 mm, 3 faces (baked)
FEATURE [Part::Feature] Part__Feature158  label="XC7A35T-L1CSG324I158"
  shape: bbox 0.45 x 0.45 x 0.45 mm, 3 faces (baked)
FEATURE [Part::Feature] Part__Feature159  label="XC7A35T-L1CSG324I159"
  shape: bbox 0.45 x 0.45 x 0.45 mm, 3 faces (baked)
FEATURE [Part::Feature] Part__Feature160  label="XC7A35T-L1CSG324I160"
  shape: bbox 0.45 x 0.45 x 0.45 mm, 3 faces (baked)
FEATURE [Part::Feature] Part__Feature161  label="XC7A35T-L1CSG324I161"
  shape: bbox 0.45 x 0.45 x 0.45 mm, 3 faces (baked)
FEATURE [Part::Feature] Part__Feature162  label="XC7A35T-L1CSG324I162"
  shape: bbox 0.45 x 0.45 x 0.45 mm, 3 faces (baked)
FEATURE [Part::Feature] Part__Feature163  label="XC7A35T-L1CSG324I163"
  shape: bbox 0.45 x 0.45 x 0.45 mm, 3 faces (baked)
FEATURE [Part::Feature] Part__Feature164  label="XC7A35T-L1CSG324I164"
  shape: bbox 0.45 x 0.45 x 0.45 mm, 3 faces (baked)
FEATURE [Part::Feature] Part__Feature165  label="XC7A35T-L1CSG324I165"
  shape: bbox 0.45 x 0.45 x 0.45 mm, 3 faces (baked)
FEATURE [Part::Feature] Part__Feature166  label="XC7A35T-L1CSG324I166"
  shape: bbox 0.45 x 0.45 x 0.45 mm, 3 faces (baked)
FEATURE [Part::Feature] Part__Feature167  label="XC7A35T-L1CSG324I167"
  shape: bbox 0.45 x 0.45 x 0.45 mm, 3 faces (baked)
FEATURE [Part::Feature] Part__Feature168  label="XC7A35T-L1CSG324I168"
  shape: bbox 0.45 x 0.45 x 0.45 mm, 3 faces (baked)
FEATURE [Part::Feature] Part__Feature169  label="XC7A35T-L1CSG324I169"
  shape: bbox 0.45 x 0.45 x 0.45 mm, 3 faces (baked)
FEATURE [Part::Feature] Part__Feature170  label="XC7A35T-L1CSG324I170"
  shape: bbox 0.45 x 0.45 x 0.45 mm, 3 faces (baked)
FEATURE [Part::Feature] Part__Feature171  label="XC7A35T-L1CSG324I171"
  shape: bbox 0.45 x 0.45 x 0.45 mm, 3 faces (baked)
FEATURE [Part::Feature] Part__Feature172  label="XC7A35T-L1CSG324I172"
  shape: bbox 0.45 x 0.45 x 0.45 mm, 3 faces (baked)
FEATURE [Part::Feature] Part__Feature173  label="XC7A35T-L1CSG324I173"
  shape: bbox 0.45 x 0.45 x 0.45 mm, 3 faces (baked)
FEATURE [Part::Feature] Part__Feature174  label="XC7A35T-L1CSG324I174"
  shape: bbox 0.45 x 0.45 x 0.45 mm, 3 faces (baked)
FEATURE [Part::Feature] Part__Feature175  label="XC7A35T-L1CSG324I175"
  shape: bbox 0.45 x 0.45 x 0.45 mm, 3 faces (baked)
FEATURE [Part::Feature] Part__Feature176  label="XC7A35T-L1CSG324I176"
  shape: bbox 0.45 x 0.45 x 0.45 mm, 3 faces (baked)
FEATURE [Part::Feature] Part__Feature177  label="XC7A35T-L1CSG324I177"
  shape: bbox 0.45 x 0.45 x 0.45 mm, 3 faces (baked)
FEATURE [Part::Feature] Part__Feature178  label="XC7A35T-L1CSG324I178"
  shape: bbox 0.45 x 0.45 x 0.45 mm, 3 faces (baked)
FEATURE [Part::Feature] Part__Feature179  label="XC7A35T-L1CSG324I179"
  shape: bbox 0.45 x 0.45 x 0.45 mm, 3 faces (baked)
FEATURE [Part::Feature] Part__Feature180  label="XC7A35T-L1CSG324I180"
  shape: bbox 0.45 x 0.45 x 0.45 mm, 3 faces (baked)
FEATURE [Part::Feature] Part__Feature181  label="XC7A35T-L1CSG324I181"
  shape: bbox 0.45 x 0.45 x 0.45 mm, 3 faces (baked)
FEATURE [Part::Feature] Part__Feature182  label="XC7A35T-L1CSG324I182"
  shape: bbox 0.45 x 0.45 x 0.45 mm, 3 faces (baked)
FEATURE [Part::Feature] Part__Feature183  label="XC7A35T-L1CSG324I183"
  shape: bbox 0.45 x 0.45 x 0.45 mm, 3 faces (baked)
FEATURE [Part::Feature] Part__Feature184  label="XC7A35T-L1CSG324I184"
  shape: bbox 0.45 x 0.45 x 0.45 mm, 3 faces (baked)
FEATURE [Part::Feature] Part__Feature185  label="XC7A35T-L1CSG324I185"
  shape: bbox 0.45 x 0.45 x 0.45 mm, 3 faces (baked)
FEATURE [Part::Feature] Part__Feature186  label="XC7A35T-L1CSG324I186"
  shape: bbox 0.45 x 0.45 x 0.45 mm, 3 faces (baked)
FEATURE [Part::Feature] Part__Feature187  label="XC7A35T-L1CSG324I187"
  shape: bbox 0.45 x 0.45 x 0.45 mm, 3 faces (baked)
FEATURE [Part::Feature] Part__Feature188  label="XC7A35T-L1CSG324I188"
  shape: bbox 0.45 x 0.45 x 0.45 mm, 3 faces (baked)
FEATURE [Part::Feature] Part__Feature189  label="XC7A35T-L1CSG324I189"
  shape: bbox 0.45 x 0.45 x 0.45 mm, 3 faces (baked)
FEATURE [Part::Feature] Part__Feature190  label="XC7A35T-L1CSG324I190"
  shape: bbox 0.45 x 0.45 x 0.45 mm, 3 faces (baked)
FEATURE [Part::Feature] Part__Feature191  label="XC7A35T-L1CSG324I191"
  shape: bbox 0.45 x 0.45 x 0.45 mm, 3 faces (baked)
FEATURE [Part::Feature] Part__Feature192  label="XC7A35T-L1CSG324I192"
  shape: bbox 0.45 x 0.45 x 0.45 mm, 3 faces (baked)
FEATURE [Part::Feature] Part__Feature193  label="XC7A35T-L1CSG324I193"
  shape: bbox 0.45 x 0.45 x 0.45 mm, 3 faces (baked)
FEATURE [Part::Feature] Part__Feature194  label="XC7A35T-L1CSG324I194"
  shape: bbox 0.45 x 0.45 x 0.45 mm, 3 faces (baked)
FEATURE [Part::Feature] Part__Feature195  label="XC7A35T-L1CSG324I195"
  shape: bbox 0.45 x 0.45 x 0.45 mm, 3 faces (baked)
FEATURE [Part::Feature] Part__Feature196  label="XC7A35T-L1CSG324I196"
  shape: bbox 0.45 x 0.45 x 0.45 mm, 3 faces (baked)
FEATURE [Part::Feature] Part__Feature197  label="XC7A35T-L1CSG324I197"
  shape: bbox 0.45 x 0.45 x 0.45 mm, 3 faces (baked)
FEATURE [Part::Feature] Part__Feature198  label="XC7A35T-L1CSG324I198"
  shape: bbox 0.45 x 0.45 x 0.45 mm, 3 faces (baked)
FEATURE [Part::Feature] Part__Feature199  label="XC7A35T-L1CSG324I199"
  shape: bbox 0.45 x 0.45 x 0.45 mm, 3 faces (baked)
FEATURE [Part::Feature] Part__Feature200  label="XC7A35T-L1CSG324I200"
  shape: bbox 0.45 x 0.45 x 0.45 mm, 3 faces (baked)
FEATURE [Part::Feature] Part__Feature201  label="XC7A35T-L1CSG324I201"
  shape: bbox 0.45 x 0.45 x 0.45 mm, 3 faces (baked)
FEATURE [Part::Feature] Part__Feature202  label="XC7A35T-L1CSG324I202"
  shape: bbox 0.45 x 0.45 x 0.45 mm, 3 faces (baked)
FEATURE [Part::Feature] Part__Feature203  label="XC7A35T-L1CSG324I203"
  shape: bbox 0.45 x 0.45 x 0.45 mm, 3 faces (baked)
FEATURE [Part::Feature] Part__Feature204  label="XC7A35T-L1CSG324I204"
  shape: bbox 0.45 x 0.45 x 0.45 mm, 3 faces (baked)
FEATURE [Part::Feature] Part__Feature205  label="XC7A35T-L1CSG324I205"
  shape: bbox 0.45 x 0.45 x 0.45 mm, 3 faces (baked)
FEATURE [Part::Feature] Part__Feature206  label="XC7A35T-L1CSG324I206"
  shape: bbox 0.45 x 0.45 x 0.45 mm, 3 faces (baked)
FEATURE [Part::Feature] Part__Feature207  label="XC7A35T-L1CSG324I207"
  shape: bbox 0.45 x 0.45 x 0.45 mm, 3 faces (baked)
FEATURE [Part::Feature] Part__Feature208  label="XC7A35T-L1CSG324I208"
  shape: bbox 0.45 x 0.45 x 0.45 mm, 3 faces (baked)
FEATURE [Part::Feature] Part__Feature209  label="XC7A35T-L1CSG324I209"
  shape: bbox 0.45 x 0.45 x 0.45 mm, 3 faces (baked)
FEATURE [Part::Feature] Part__Feature210  label="XC7A35T-L1CSG324I210"
  shape: bbox 0.45 x 0.45 x 0.45 mm, 3 faces (baked)
FEATURE [Part::Feature] Part__Feature211  label="XC7A35T-L1CSG324I211"
  shape: bbox 0.45 x 0.45 x 0.45 mm, 3 faces (baked)
FEATURE [Part::Feature] Part__Feature212  label="XC7A35T-L1CSG324I212"
  shape: bbox 0.45 x 0.45 x 0.45 mm, 3 faces (baked)
FEATURE [Part::Feature] Part__Feature213  label="XC7A35T-L1CSG324I213"
  shape: bbox 0.45 x 0.45 x 0.45 mm, 3 faces (baked)
FEATURE [Part::Feature] Part__Feature214  label="XC7A35T-L1CSG324I214"
  shape: bbox 0.45 x 0.45 x 0.45 mm, 3 faces (baked)
FEATURE [Part::Feature] Part__Feature215  label="XC7A35T-L1CSG324I215"
  shape: bbox 0.45 x 0.45 x 0.45 mm, 3 faces (baked)
FEATURE [Part::Feature] Part__Feature216  label="XC7A35T-L1CSG324I216"
  shape: bbox 0.45 x 0.45 x 0.45 mm, 3 faces (baked)
FEATURE [Part::Feature] Part__Feature217  label="XC7A35T-L1CSG324I217"
  shape: bbox 0.45 x 0.45 x 0.45 mm, 3 faces (baked)
FEATURE [Part::Feature] Part__Feature218  label="XC7A35T-L1CSG324I218"
  shape: bbox 0.45 x 0.45 x 0.45 mm, 3 faces (baked)
FEATURE [Part::Feature] Part__Feature219  label="XC7A35T-L1CSG324I219"
  shape: bbox 0.45 x 0.45 x 0.45 mm, 3 faces (baked)
FEATURE [Part::Feature] Part__Feature220  label="XC7A35T-L1CSG324I220"
  shape: bbox 0.45 x 0.45 x 0.45 mm, 3 faces (baked)
FEATURE [Part::Feature] Part__Feature221  label="XC7A35T-L1CSG324I221"
  shape: bbox 0.45 x 0.45 x 0.45 mm, 3 faces (baked)
FEATURE [Part::Feature] Part__Feature222  label="XC7A35T-L1CSG324I222"
  shape: bbox 0.45 x 0.45 x 0.45 mm, 3 faces (baked)
FEATURE [Part::Feature] Part__Feature223  label="XC7A35T-L1CSG324I223"
  shape: bbox 0.45 x 0.45 x 0.45 mm, 3 faces (baked)
FEATURE [Part::Feature] Part__Feature224  label="XC7A35T-L1CSG324I224"
  shape: bbox 0.45 x 0.45 x 0.45 mm, 3 faces (baked)
FEATURE [Part::Feature] Part__Feature225  label="XC7A35T-L1CSG324I225"
  shape: bbox 0.45 x 0.45 x 0.45 mm, 3 faces (baked)
FEATURE [Part::Feature] Part__Feature226  label="XC7A35T-L1CSG324I226"
  shape: bbox 0.45 x 0.45 x 0.45 mm, 3 faces (baked)
FEATURE [Part::Feature] Part__Feature227  label="XC7A35T-L1CSG324I227"
  shape: bbox 0.45 x 0.45 x 0.45 mm, 3 faces (baked)
FEATURE [Part::Feature] Part__Feature228  label="XC7A35T-L1CSG324I228"
  shape: bbox 0.45 x 0.45 x 0.45 mm, 3 faces (baked)
FEATURE [Part::Feature] Part__Feature229  label="XC7A35T-L1CSG324I229"
  shape: bbox 0.45 x 0.45 x 0.45 mm, 3 faces (baked)
FEATURE [Part::Feature] Part__Feature230  label="XC7A35T-L1CSG324I230"
  shape: bbox 0.45 x 0.45 x 0.45 mm, 3 faces (baked)
FEATURE [Part::Feature] Part__Feature231  label="XC7A35T-L1CSG324I231"
  shape: bbox 0.45 x 0.45 x 0.45 mm, 3 faces (baked)
FEATURE [Part::Feature] Part__Feature232  label="XC7A35T-L1CSG324I232"
  shape: bbox 0.45 x 0.45 x 0.45 mm, 3 faces (baked)
FEATURE [Part::Feature] Part__Feature233  label="XC7A35T-L1CSG324I233"
  shape: bbox 0.45 x 0.45 x 0.45 mm, 3 faces (baked)
FEATURE [Part::Feature] Part__Feature234  label="XC7A35T-L1CSG324I234"
  shape: bbox 0.45 x 0.45 x 0.45 mm, 3 faces (baked)
FEATURE [Part::Feature] Part__Feature235  label="XC7A35T-L1CSG324I235"
  shape: bbox 0.45 x 0.45 x 0.45 mm, 3 faces (baked)
FEATURE [Part::Feature] Part__Feature236  label="XC7A35T-L1CSG324I236"
  shape: bbox 0.45 x 0.45 x 0.45 mm, 3 faces (baked)
FEATURE [Part::Feature] Part__Feature237  label="XC7A35T-L1CSG324I237"
  shape: bbox 0.45 x 0.45 x 0.45 mm, 3 faces (baked)
FEATURE [Part::Feature] Part__Feature238  label="XC7A35T-L1CSG324I238"
  shape: bbox 0.45 x 0.45 x 0.45 mm, 3 faces (baked)
FEATURE [Part::Feature] Part__Feature239  label="XC7A35T-L1CSG324I239"
  shape: bbox 0.45 x 0.45 x 0.45 mm, 3 faces (baked)
FEATURE [Part::Feature] Part__Feature240  label="XC7A35T-L1CSG324I240"
  shape: bbox 0.45 x 0.45 x 0.45 mm, 3 faces (baked)
FEATURE [Part::Feature] Part__Feature241  label="XC7A35T-L1CSG324I241"
  shape: bbox 0.45 x 0.45 x 0.45 mm, 3 faces (baked)
FEATURE [Part::Feature] Part__Feature242  label="XC7A35T-L1CSG324I242"
  shape: bbox 0.45 x 0.45 x 0.45 mm, 3 faces (baked)
FEATURE [Part::Feature] Part__Feature243  label="XC7A35T-L1CSG324I243"
  shape: bbox 0.45 x 0.45 x 0.45 mm, 3 faces (baked)
FEATURE [Part::Feature] Part__Feature244  label="XC7A35T-L1CSG324I244"
  shape: bbox 0.45 x 0.45 x 0.45 mm, 3 faces (baked)
FEATURE [Part::Feature] Part__Feature245  label="XC7A35T-L1CSG324I245"
  shape: bbox 0.45 x 0.45 x 0.45 mm, 3 faces (baked)
FEATURE [Part::Feature] Part__Feature246  label="XC7A35T-L1CSG324I246"
  shape: bbox 0.45 x 0.45 x 0.45 mm, 3 faces (baked)
FEATURE [Part::Feature] Part__Feature247  label="XC7A35T-L1CSG324I247"
  shape: bbox 0.45 x 0.45 x 0.45 mm, 3 faces (baked)
FEATURE [Part::Feature] Part__Feature248  label="XC7A35T-L1CSG324I248"
  shape: bbox 0.45 x 0.45 x 0.45 mm, 3 faces (baked)
FEATURE [Part::Feature] Part__Feature249  label="XC7A35T-L1CSG324I249"
  shape: bbox 0.45 x 0.45 x 0.45 mm, 3 faces (baked)
FEATURE [Part::Feature] Part__Feature250  label="XC7A35T-L1CSG324I250"
  shape: bbox 0.45 x 0.45 x 0.45 mm, 3 faces (baked)
FEATURE [Part::Feature] Part__Feature251  label="XC7A35T-L1CSG324I251"
  shape: bbox 0.45 x 0.45 x 0.45 mm, 3 faces (baked)
FEATURE [Part::Feature] Part__Feature252  label="XC7A35T-L1CSG324I252"
  shape: bbox 0.45 x 0.45 x 0.45 mm, 3 faces (baked)
FEATURE [Part::Feature] Part__Feature253  label="XC7A35T-L1CSG324I253"
  shape: bbox 0.45 x 0.45 x 0.45 mm, 3 faces (baked)
FEATURE [Part::Feature] Part__Feature254  label="XC7A35T-L1CSG324I254"
  shape: bbox 0.45 x 0.45 x 0.45 mm, 3 faces (baked)
FEATURE [Part::Feature] Part__Feature255  label="XC7A35T-L1CSG324I255"
  shape: bbox 0.45 x 0.45 x 0.45 mm, 3 faces (baked)
FEATURE [Part::Feature] Part__Feature256  label="XC7A35T-L1CSG324I256"
  shape: bbox 0.45 x 0.45 x 0.45 mm, 3 faces (baked)
FEATURE [Part::Feature] Part__Feature257  label="XC7A35T-L1CSG324I257"
  shape: bbox 0.45 x 0.45 x 0.45 mm, 3 faces (baked)
FEATURE [Part::Feature] Part__Feature258  label="XC7A35T-L1CSG324I258"
  shape: bbox 0.45 x 0.45 x 0.45 mm, 3 faces (baked)
FEATURE [Part::Feature] Part__Feature259  label="XC7A35T-L1CSG324I259"
  shape: bbox 0.45 x 0.45 x 0.45 mm, 3 faces (baked)
FEATURE [Part::Feature] Part__Feature260  label="XC7A35T-L1CSG324I260"
  shape: bbox 0.45 x 0.45 x 0.45 mm, 3 faces (baked)
FEATURE [Part::Feature] Part__Feature261  label="XC7A35T-L1CSG324I261"
  shape: bbox 0.45 x 0.45 x 0.45 mm, 3 faces (baked)
FEATURE [Part::Feature] Part__Feature262  label="XC7A35T-L1CSG324I262"
  shape: bbox 0.45 x 0.45 x 0.45 mm, 3 faces (baked)
FEATURE [Part::Feature] Part__Feature263  label="XC7A35T-L1CSG324I263"
  shape: bbox 0.45 x 0.45 x 0.45 mm, 3 faces (baked)
FEATURE [Part::Feature] Part__Feature264  label="XC7A35T-L1CSG324I264"
  shape: bbox 0.45 x 0.45 x 0.45 mm, 3 faces (baked)
FEATURE [Part::Feature] Part__Feature265  label="XC7A35T-L1CSG324I265"
  shape: bbox 0.45 x 0.45 x 0.45 mm, 3 faces (baked)
FEATURE [Part::Feature] Part__Feature266  label="XC7A35T-L1CSG324I266"
  shape: bbox 0.45 x 0.45 x 0.45 mm, 3 faces (baked)
FEATURE [Part::Feature] Part__Feature267  label="XC7A35T-L1CSG324I267"
  shape: bbox 0.45 x 0.45 x 0.45 mm, 3 faces (baked)
FEATURE [Part::Feature] Part__Feature268  label="XC7A35T-L1CSG324I268"
  shape: bbox 0.45 x 0.45 x 0.45 mm, 3 faces (baked)
FEATURE [Part::Feature] Part__Feature269  label="XC7A35T-L1CSG324I269"
  shape: bbox 0.45 x 0.45 x 0.45 mm, 3 faces (baked)
FEATURE [Part::Feature] Part__Feature270  label="XC7A35T-L1CSG324I270"
  shape: bbox 0.45 x 0.45 x 0.45 mm, 3 faces (baked)
FEATURE [Part::Feature] Part__Feature271  label="XC7A35T-L1CSG324I271"
  shape: bbox 0.45 x 0.45 x 0.45 mm, 3 faces (baked)
FEATURE [Part::Feature] Part__Feature272  label="XC7A35T-L1CSG324I272"
  shape: bbox 0.45 x 0.45 x 0.45 mm, 3 faces (baked)
FEATURE [Part::Feature] Part__Feature273  label="XC7A35T-L1CSG324I273"
  shape: bbox 0.45 x 0.45 x 0.45 mm, 3 faces (baked)
FEATURE [Part::Feature] Part__Feature274  label="XC7A35T-L1CSG324I274"
  shape: bbox 0.45 x 0.45 x 0.45 mm, 3 faces (baked)
FEATURE [Part::Feature] Part__Feature275  label="XC7A35T-L1CSG324I275"
  shape: bbox 0.45 x 0.45 x 0.45 mm, 3 faces (baked)
FEATURE [Part::Feature] Part__Feature276  label="XC7A35T-L1CSG324I276"
  shape: bbox 0.45 x 0.45 x 0.45 mm, 3 faces (baked)
FEATURE [Part::Feature] Part__Feature277  label="XC7A35T-L1CSG324I277"
  shape: bbox 0.45 x 0.45 x 0.45 mm, 3 faces (baked)
FEATURE [Part::Feature] Part__Feature278  label="XC7A35T-L1CSG324I278"
  shape: bbox 0.45 x 0.45 x 0.45 mm, 3 faces (baked)
FEATURE [Part::Feature] Part__Feature279  label="XC7A35T-L1CSG324I279"
  shape: bbox 0.45 x 0.45 x 0.45 mm, 3 faces (baked)
FEATURE [Part::Feature] Part__Feature280  label="XC7A35T-L1CSG324I280"
  shape: bbox 0.45 x 0.45 x 0.45 mm, 3 faces (baked)
FEATURE [Part::Feature] Part__Feature281  label="XC7A35T-L1CSG324I281"
  shape: bbox 0.45 x 0.45 x 0.45 mm, 3 faces (baked)
FEATURE [Part::Feature] Part__Feature282  label="XC7A35T-L1CSG324I282"
  shape: bbox 0.45 x 0.45 x 0.45 mm, 3 faces (baked)
FEATURE [Part::Feature] Part__Feature283  label="XC7A35T-L1CSG324I283"
  shape: bbox 0.45 x 0.45 x 0.45 mm, 3 faces (baked)
FEATURE [Part::Feature] Part__Feature284  label="XC7A35T-L1CSG324I284"
  shape: bbox 0.45 x 0.45 x 0.45 mm, 3 faces (baked)
FEATURE [Part::Feature] Part__Feature285  label="XC7A35T-L1CSG324I285"
  shape: bbox 0.45 x 0.45 x 0.45 mm, 3 faces (baked)
FEATURE [Part::Feature] Part__Feature286  label="XC7A35T-L1CSG324I286"
  shape: bbox 0.45 x 0.45 x 0.45 mm, 3 faces (baked)
FEATURE [Part::Feature] Part__Feature287  label="XC7A35T-L1CSG324I287"
  shape: bbox 0.45 x 0.45 x 0.45 mm, 3 faces (baked)
FEATURE [Part::Feature] Part__Feature288  label="XC7A35T-L1CSG324I288"
  shape: bbox 0.45 x 0.45 x 0.45 mm, 3 faces (baked)
FEATURE [Part::Feature] Part__Feature289  label="XC7A35T-L1CSG324I289"
  shape: bbox 0.45 x 0.45 x 0.45 mm, 3 faces (baked)
FEATURE [Part::Feature] Part__Feature290  label="XC7A35T-L1CSG324I290"
  shape: bbox 0.45 x 0.45 x 0.45 mm, 3 faces (baked)
FEATURE [Part::Feature] Part__Feature291  label="XC7A35T-L1CSG324I291"
  shape: bbox 0.45 x 0.45 x 0.45 mm, 3 faces (baked)
FEATURE [Part::Feature] Part__Feature292  label="XC7A35T-L1CSG324I292"
  shape: bbox 0.45 x 0.45 x 0.45 mm, 3 faces (baked)
FEATURE [Part::Feature] Part__Feature293  label="XC7A35T-L1CSG324I293"
  shape: bbox 0.45 x 0.45 x 0.45 mm, 3 faces (baked)
FEATURE [Part::Feature] Part__Feature294  label="XC7A35T-L1CSG324I294"
  shape: bbox 0.45 x 0.45 x 0.45 mm, 3 faces (baked)
FEATURE [Part::Feature] Part__Feature295  label="XC7A35T-L1CSG324I295"
  shape: bbox 0.45 x 0.45 x 0.45 mm, 3 faces (baked)
FEATURE [Part::Feature] Part__Feature296  label="XC7A35T-L1CSG324I296"
  shape: bbox 0.45 x 0.45 x 0.45 mm, 3 faces (baked)
FEATURE [Part::Feature] Part__Feature297  label="XC7A35T-L1CSG324I297"
  shape: bbox 0.45 x 0.45 x 0.45 mm, 3 faces (baked)
FEATURE [Part::Feature] Part__Feature298  label="XC7A35T-L1CSG324I298"
  shape: bbox 0.45 x 0.45 x 0.45 mm, 3 faces (baked)
FEATURE [Part::Feature] Part__Feature299  label="XC7A35T-L1CSG324I299"
  shape: bbox 0.45 x 0.45 x 0.45 mm, 3 faces (baked)
FEATURE [Part::Feature] Part__Feature300  label="XC7A35T-L1CSG324I300"
  shape: bbox 0.45 x 0.45 x 0.45 mm, 3 faces (baked)
FEATURE [Part::Feature] Part__Feature301  label="XC7A35T-L1CSG324I301"
  shape: bbox 0.45 x 0.45 x 0.45 mm, 3 faces (baked)
FEATURE [Part::Feature] Part__Feature302  label="XC7A35T-L1CSG324I302"
  shape: bbox 0.45 x 0.45 x 0.45 mm, 3 faces (baked)
FEATURE [Part::Feature] Part__Feature303  label="XC7A35T-L1CSG324I303"
  shape: bbox 0.45 x 0.45 x 0.45 mm, 3 faces (baked)
FEATURE [Part::Feature] Part__Feature304  label="XC7A35T-L1CSG324I304"
  shape: bbox 0.45 x 0.45 x 0.45 mm, 3 faces (baked)
FEATURE [Part::Feature] Part__Feature305  label="XC7A35T-L1CSG324I305"
  shape: bbox 0.45 x 0.45 x 0.45 mm, 3 faces (baked)
FEATURE [Part::Feature] Part__Feature306  label="XC7A35T-L1CSG324I306"
  shape: bbox 0.45 x 0.45 x 0.45 mm, 3 faces (baked)
FEATURE [Part::Feature] Part__Feature307  label="XC7A35T-L1CSG324I307"
  shape: bbox 0.45 x 0.45 x 0.45 mm, 3 faces (baked)
FEATURE [Part::Feature] Part__Feature308  label="XC7A35T-L1CSG324I308"
  shape: bbox 0.45 x 0.45 x 0.45 mm, 3 faces (baked)
FEATURE [Part::Feature] Part__Feature309  label="XC7A35T-L1CSG324I309"
  shape: bbox 0.45 x 0.45 x 0.45 mm, 3 faces (baked)
FEATURE [Part::Feature] Part__Feature310  label="XC7A35T-L1CSG324I310"
  shape: bbox 0.45 x 0.45 x 0.45 mm, 3 faces (baked)
FEATURE [Part::Feature] Part__Feature311  label="XC7A35T-L1CSG324I311"
  shape: bbox 0.45 x 0.45 x 0.45 mm, 3 faces (baked)
FEATURE [Part::Feature] Part__Feature312  label="XC7A35T-L1CSG324I312"
  shape: bbox 0.45 x 0.45 x 0.45 mm, 3 faces (baked)
FEATURE [Part::Feature] Part__Feature313  label="XC7A35T-L1CSG324I313"
  shape: bbox 0.45 x 0.45 x 0.45 mm, 3 faces (baked)
FEATURE [Part::Feature] Part__Feature314  label="XC7A35T-L1CSG324I314"
  shape: bbox 0.45 x 0.45 x 0.45 mm, 3 faces (baked)
FEATURE [Part::Feature] Part__Feature315  label="XC7A35T-L1CSG324I315"
  shape: bbox 0.45 x 0.45 x 0.45 mm, 3 faces (baked)
FEATURE [Part::Feature] Part__Feature316  label="XC7A35T-L1CSG324I316"
  shape: bbox 0.45 x 0.45 x 0.45 mm, 3 faces (baked)
FEATURE [Part::Feature] Part__Feature317  label="XC7A35T-L1CSG324I317"
  shape: bbox 0.45 x 0.45 x 0.45 mm, 3 faces (baked)
FEATURE [Part::Feature] Part__Feature318  label="XC7A35T-L1CSG324I318"
  shape: bbox 0.45 x 0.45 x 0.45 mm, 3 faces (baked)
FEATURE [Part::Feature] Part__Feature319  label="XC7A35T-L1CSG324I319"
  shape: bbox 0.45 x 0.45 x 0.45 mm, 3 faces (baked)
FEATURE [Part::Feature] Part__Feature320  label="XC7A35T-L1CSG324I320"
  shape: bbox 0.45 x 0.45 x 0.45 mm, 3 faces (baked)
FEATURE [Part::Feature] Part__Feature321  label="XC7A35T-L1CSG324I321"
  shape: bbox 0.45 x 0.45 x 0.45 mm, 3 faces (baked)
FEATURE [Part::Feature] Part__Feature322  label="XC7A35T-L1CSG324I322"
  shape: bbox 0.45 x 0.45 x 0.45 mm, 3 faces (baked)
FEATURE [Part::Feature] Part__Feature323  label="XC7A35T-L1CSG324I323"
  shape: bbox 0.45 x 0.45 x 0.45 mm, 3 faces (baked)
FEATURE [Part::Feature] Part__Feature324  label="XC7A35T-L1CSG324I324"
  shape: bbox 0.45 x 0.45 x 0.45 mm, 3 faces (baked)
FEATURE [App::Part] XC7A35T_L1CSG324I  label="REF_XC7A35T-L1CSG324I325_4182825f526f"
  Group = -> [Part__Feature,Part__Feature001,Part__Feature002,Part__Feature003,Part__Feature004,Part__Feature005,Part__Feature006,Part__Feature007,Part__Feature008,Part__Feature009,Part__Feature010,Part__Feature011,Part__Feature012,Part__Feature013,Part__Feature014,Part__Feature015,Part__Feature016,Part__Feature017,Part__Feature018,Part__Feature019,Part__Feature020,Part__Feature021,Part__Feature022,+302 more]
  Origin = -> Origin008
  Placement = pos=(27.6627,-26.7284,0) rot=(0.862856,0.357407,0.357407;1.71777rad)
FEATURE [App::Link] REF_LED_0805_2012Metric_89f5d563d29e_ln_001  label="REF_REF_LED_0805_2012Metric_0b573702dffd"
  LinkPlacement = pos=(1.4,-9.7,0) rot=(0,0,1;0rad)
  LinkedObject = -> Shape003
  Placement = pos=(1.4,-9.7,0) rot=(0,0,1;0rad)
FEATURE [App::Link] REF_C_1206_3216Metric_fe751edea67d_ln_003  label="REF_REF_C_1206_3216Metric_9f94975ac2a3"
  LinkPlacement = pos=(15.2,-20.2,0) rot=(0,0,1;0rad)
  LinkedObject = -> Shape001
  Placement = pos=(15.2,-20.2,0) rot=(0,0,1;0rad)
FEATURE [App::Link] REF_C_0805_2012Metric_293c7b1e92e5_ln_004  label="REF_REF_C_0805_2012Metric_4dbba0a734f5"
  LinkPlacement = pos=(25.8,-43.7,0) rot=(0,0,1;0rad)
  LinkedObject = -> Shape002
  Placement = pos=(25.8,-43.7,0) rot=(0,0,1;0rad)
FEATURE [Part::Feature] Shape008  label="REF_PinHeader_1x06_P254mm_Vertical_93db46f388f3"
  Placement = pos=(48.26,-46.84,0) rot=(0,0,1;1.5708rad)
  shape: bbox 15.24 x 2.54 x 11.54 mm, 148 faces (baked)
FEATURE [App::Link] REF_C_1206_3216Metric_fe751edea67d_ln_004  label="REF_REF_C_1206_3216Metric_195d526c249b"
  LinkPlacement = pos=(1.2,-32.3,0) rot=(0,0,1;0rad)
  LinkedObject = -> Shape001
  Placement = pos=(1.2,-32.3,0) rot=(0,0,1;0rad)
FEATURE [Part::Feature] Shape009  label="REF_SOT_23_6_65366ad05450"
  Placement = pos=(12.8625,-31.25,0) rot=(0,0,1;0rad)
  shape: bbox 2.8 x 2.9 x 1.55 mm, 124 faces (baked)
FEATURE [App::Link] REF_R_0603_1608Metric_0f1490cb362e_ln_009  label="REF_REF_R_0603_1608Metric_3104923b1317"
  LinkPlacement = pos=(51.775,-11,0) rot=(0,0,1;0rad)
  LinkedObject = -> Shape
  Placement = pos=(51.775,-11,0) rot=(0,0,1;0rad)
FEATURE [App::Link] REF_TSOT_23_5_5b1d7019fdeb_ln_  label="REF_REF_TSOT_23_5_82a51ceb518d"
  LinkPlacement = pos=(1.6,-27.4,0) rot=(0,0,1;1.5708rad)
  LinkedObject = -> Shape005
  Placement = pos=(1.6,-27.4,0) rot=(0,0,1;1.5708rad)
FEATURE [App::Link] REF_C_1206_3216Metric_fe751edea67d_ln_005  label="REF_REF_C_1206_3216Metric_afcf5dd0421e"
  LinkPlacement = pos=(13,-37.4,0) rot=(0,0,1;0rad)
  LinkedObject = -> Shape001
  Placement = pos=(13,-37.4,0) rot=(0,0,1;0rad)
FEATURE [App::Link] REF_R_0603_1608Metric_0f1490cb362e_ln_010  label="REF_REF_R_0603_1608Metric_103e346e62a0"
  LinkPlacement = pos=(50.4,-43.6,0) rot=(0,0,1;1.5708rad)
  LinkedObject = -> Shape
  Placement = pos=(50.4,-43.6,0) rot=(0,0,1;1.5708rad)
FEATURE [App::Link] REF_R_0603_1608Metric_0f1490cb362e_ln_011  label="REF_REF_R_0603_1608Metric_854742afb018"
  LinkPlacement = pos=(53.3,-43.6,0) rot=(0,0,1;1.5708rad)
  LinkedObject = -> Shape
  Placement = pos=(53.3,-43.6,0) rot=(0,0,1;1.5708rad)
FEATURE [App::Link] REF_C_1206_3216Metric_fe751edea67d_ln_006  label="REF_REF_C_1206_3216Metric_b095e735b3e0"
  LinkPlacement = pos=(13,-35,0) rot=(0,0,1;0rad)
  LinkedObject = -> Shape001
  Placement = pos=(13,-35,0) rot=(0,0,1;0rad)
FEATURE [App::Link] REF_R_0603_1608Metric_0f1490cb362e_ln_012  label="REF_REF_R_0603_1608Metric_a4058f385080"
  LinkPlacement = pos=(48.8,-43.6,0) rot=(0,0,1;1.5708rad)
  LinkedObject = -> Shape
  Placement = pos=(48.8,-43.6,0) rot=(0,0,1;1.5708rad)
FEATURE [App::Link] REF_C_0805_2012Metric_293c7b1e92e5_ln_005  label="REF_REF_C_0805_2012Metric_83bef9c6ee82"
  LinkPlacement = pos=(60.6,-29.6,0) rot=(0,0,1;1.5708rad)
  LinkedObject = -> Shape002
  Placement = pos=(60.6,-29.6,0) rot=(0,0,1;1.5708rad)
FEATURE [App::Link] REF_LED_0805_2012Metric_89f5d563d29e_ln_002  label="REF_REF_LED_0805_2012Metric_fe9c539bbdcb"
  LinkPlacement = pos=(1.4,-6.7,0) rot=(0,0,1;0rad)
  LinkedObject = -> Shape003
  Placement = pos=(1.4,-6.7,0) rot=(0,0,1;0rad)
FEATURE [App::Link] REF_R_0603_1608Metric_0f1490cb362e_ln_013  label="REF_REF_R_0603_1608Metric_f2cb1367ab51"
  LinkPlacement = pos=(41.2,-14.2,0) rot=(0,0,1;0.785398rad)
  LinkedObject = -> Shape
  Placement = pos=(41.2,-14.2,0) rot=(0,0,1;0.785398rad)
FEATURE [App::Part] Top_4879
  Group = -> [Shape,Shape001,REF_R_0603_1608Metric_0f1490cb362e_ln_,REF_R_0603_1608Metric_0f1490cb362e_ln_001,REF_R_0603_1608Metric_0f1490cb362e_ln_002,Shape002,REF_C_0805_2012Metric_293c7b1e92e5_ln_,REF_R_0603_1608Metric_0f1490cb362e_ln_003,REF_R_0603_1608Metric_0f1490cb362e_ln_004,Shape003,REF_C_0805_2012Metric_293c7b1e92e5_ln_001,Shape004,REF_R_0603_1608Metric_0f1490cb362e_ln_005,+30 more]
  Origin = -> Origin003
FEATURE [Part::Feature] Shape010  label="REF_PinHeader_2x25_P254mm_Vertical_ddf9f30e997e"
  Placement = pos=(2e-16,0,-1.6) rot=(0.707107,-0.707107,0;3.14159rad)
  shape: bbox 63.5 x 5.08 x 11.54 mm, 1054 faces (baked)
FEATURE [App::Link] REF_PinHeader_2x25_P254mm_Vertical_ddf9f30e997e_ln_  label="REF_REF_PinHeader_2x25_P254mm_Vertical_182444d358db"
  LinkPlacement = pos=(2e-16,-50.84,-1.6) rot=(0.707107,-0.707107,0;3.14159rad)
  LinkedObject = -> Shape010
  Placement = pos=(2e-16,-50.84,-1.6) rot=(0.707107,-0.707107,0;3.14159rad)
FEATURE [App::Part] Bot_4879
  Group = -> [Shape010,REF_PinHeader_2x25_P254mm_Vertical_ddf9f30e997e_ln_]
  Origin = -> Origin004
FEATURE [App::Part] Step_Models_4879
  Group = -> [Top_4879,Bot_4879]
  Origin = -> Origin002
FEATURE [App::Part] Board_4879  label="fpga"
  Group = -> [Local_CS_4879,Board_Geoms_4879,Step_Models_4879]
  Origin = -> Origin001
COMPONENT P7 — recipe-attached ("fpga_ext_board", a linked part whose construction recipe lives in a companion FreeCAD document of the same project; that document's serialized recipe follows).
Construction recipe (the companion document, serialized — sketch geometry with constraints, then the solid features built on it; lengths are millimeters unless a unit is written):

FCSTD DOCUMENT  (FreeCAD 1.0R39109 (Git))
Label: fpga_ext_board
License: All rights reserved
LicenseURL: https://en.wikipedia.org/wiki/All_rights_reserved
objects: Part::Feature×4, App::Part×4, App::Link×3, PartDesign::CoordinateSystem×1, Sketcher::SketchObject×1
note: 7 computed .brp shape members not serialized (recipe doc carries the construction recipe); baked Part::Feature solids carry a one-line shape summary decoded from their .brp

FEATURE [PartDesign::CoordinateSystem] Local_CS_e45
  AttacherType = Attacher::AttachEngine3D
  MapMode = 2
FEATURE [Part::Feature] Pcb_e45
  shape: bbox 100 x 100 x 1.6 mm, 264 faces (baked)
FEATURE [Sketcher::SketchObject] PCB_Sketch_e45
  ArcFitTolerance = 1e-06
  FullyConstrained = false
  MakeInternals = false
  sketch-geometry (4):
    g0: LineSegment StartX=56.7 StartY=-51 StartZ=0 EndX=156.7 EndY=-51 EndZ=0
    g1: LineSegment StartX=156.7 StartY=-51 StartZ=0 EndX=156.7 EndY=-151 EndZ=0
    g2: LineSegment StartX=156.7 StartY=-151 StartZ=0 EndX=56.7 EndY=-151 EndZ=0
    g3: LineSegment StartX=56.7 StartY=-151 StartZ=0 EndX=56.7 EndY=-51 EndZ=0
  constraints (4):
    c: Coincident(g2,g3)
    c: Coincident(g0,g3)
    c: Coincident(g1,g2)
    c: Coincident(g0,g1)
FEATURE [App::Part] Board_Geoms_e45
  Group = -> [Pcb_e45,PCB_Sketch_e45]
  Origin = -> Origin
FEATURE [Part::Feature] Shape  label="J3_PinSocket_2x25_P2.54mm_Vertical_5b0326eaf643"
  Placement = pos=(80.9,-70.5,0) rot=(0,0,1;1.5708rad)
  shape: bbox 63.5 x 5.08 x 11.6 mm, 1310 faces (baked)
FEATURE [App::Link] J3_PinSocket_2x25_P2_54mm_Vertical_5b0326eaf643_ln_  label="J1_PinSocket_2x25_P2.54mm_Vertical_5e9946493b34"
  LinkPlacement = pos=(80.6,-131.6,0) rot=(0,0,1;1.5708rad)
  LinkedObject = -> Shape
  Placement = pos=(80.6,-131.6,0) rot=(0,0,1;1.5708rad)
FEATURE [App::Link] J3_PinSocket_2x25_P2_54mm_Vertical_5b0326eaf643_ln_001  label="J4_PinSocket_2x25_P2.54mm_Vertical_c0175bcf8e3d"
  LinkPlacement = pos=(76.56,-54.5,0) rot=(0,0,1;1.5708rad)
  LinkedObject = -> Shape
  Placement = pos=(76.56,-54.5,0) rot=(0,0,1;1.5708rad)
FEATURE [Part::Feature] Shape001  label="J6_PinHeader_1x08_P254mm_Vertical_e00167c7260b"
  Placement = pos=(116.14,-145.6,0) rot=(0,0,1;1.5708rad)
  shape: bbox 20.32 x 2.54 x 11.54 mm, 196 faces (baked)
FEATURE [Part::Feature] Shape002  label="J7_PinHeader_1x12_P254mm_Vertical_57171d797b48"
  Placement = pos=(151.3,-95.84,0) rot=(0,0,1;0rad)
  shape: bbox 2.54 x 30.48 x 11.54 mm, 292 faces (baked)
FEATURE [App::Link] J3_PinSocket_2x25_P2_54mm_Vertical_5b0326eaf643_ln_002  label="J2_PinSocket_2x25_P2.54mm_Vertical_ab23b89833e9"
  LinkPlacement = pos=(80.9,-121.3,0) rot=(0,0,1;1.5708rad)
  LinkedObject = -> Shape
  Placement = pos=(80.9,-121.3,0) rot=(0,0,1;1.5708rad)
FEATURE [App::Part] Top_e45
  Group = -> [Shape,J3_PinSocket_2x25_P2_54mm_Vertical_5b0326eaf643_ln_,J3_PinSocket_2x25_P2_54mm_Vertical_5b0326eaf643_ln_001,Shape001,Shape002,J3_PinSocket_2x25_P2_54mm_Vertical_5b0326eaf643_ln_002]
  Origin = -> Origin003
FEATURE [App::Part] Step_Models_e45
  Group = -> [Top_e45]
  Origin = -> Origin002
FEATURE [App::Part] Board_e45  label="fpga_ext_board"
  Group = -> [Local_CS_e45,Board_Geoms_e45,Step_Models_e45]
  Origin = -> Origin001
COMPONENT P8 — geometry summary ("front panel"; no construction recipe available for this part):
  bounding box: 217.0 x 81.0 x 12.0 mm
  tessellated surface: 14,544 triangles
  volume: 54831 mm^3 (26% of its bounding box)
  symmetry: mirror-symmetric across its z mid-plane
COMPONENT P9 — recipe-attached ("power_supply", a linked part whose construction recipe lives in a companion FreeCAD document of the same project; that document's serialized recipe follows).
Construction recipe (the companion document, serialized — sketch geometry with constraints, then the solid features built on it; lengths are millimeters unless a unit is written):

FCSTD DOCUMENT  (FreeCAD 1.0R39109 (Git))
Label: power_supply
License: All rights reserved
LicenseURL: https://en.wikipedia.org/wiki/All_rights_reserved
objects: Part::Feature×4, App::Part×4, PartDesign::CoordinateSystem×1, Sketcher::SketchObject×1
note: 7 computed .brp shape members not serialized (recipe doc carries the construction recipe); baked Part::Feature solids carry a one-line shape summary decoded from their .brp

FEATURE [PartDesign::CoordinateSystem] Local_CS_7c43
  AttacherType = Attacher::AttachEngine3D
  MapMode = 2
FEATURE [Part::Feature] Pcb_7c43
  Placement = pos=(-95.45,61.9,0) rot=(0,0,1;0rad)
  shape: bbox 100 x 45 x 1.6 mm, 32 faces (baked)
FEATURE [Sketcher::SketchObject] PCB_Sketch_7c43
  ArcFitTolerance = 1e-06
  FullyConstrained = false
  MakeInternals = false
  sketch-geometry (4):
    g0: LineSegment StartX=-5.5 StartY=5.9 StartZ=0 EndX=94.5 EndY=5.9 EndZ=0
    g1: LineSegment StartX=94.5 StartY=5.9 StartZ=0 EndX=94.5 EndY=-39.1 EndZ=0
    g2: LineSegment StartX=94.5 StartY=-39.1 StartZ=0 EndX=-5.5 EndY=-39.1 EndZ=0
    g3: LineSegment StartX=-5.5 StartY=-39.1 StartZ=0 EndX=-5.5 EndY=5.9 EndZ=0
  constraints (4):
    c: Coincident(g2,g3)
    c: Coincident(g0,g3)
    c: Coincident(g1,g2)
    c: Coincident(g0,g1)
FEATURE [App::Part] Board_Geoms_7c43
  Group = -> [Pcb_7c43,PCB_Sketch_7c43]
  Origin = -> Origin
FEATURE [Part::Feature] Shape  label="F1_A_Stelvio_Kontek_PTF78_492c52c52caa"
  Placement = pos=(-2.9,-11,0) rot=(0,0,1;0rad)
  shape: bbox 24.4 x 9.4 x 15 mm, 53 faces (baked)
FEATURE [Part::Feature] Shape001  label="C2_CP_Radial_D50mm_P250mm_59ec8646bf87"
  Placement = pos=(87.9949,-23.5,0) rot=(0,0,1;0rad)
  shape: bbox 6.128 x 6.515 x 7 mm, 49 faces (baked)
FEATURE [Part::Feature] Shape002  label="PS1_Converter_ACDC_Hi-Link_HLK-20Mxx_0653979e349d"
  Placement = pos=(27.0425,-7.9425,0) rot=(0,0,1;0rad)
  shape: bbox 57.5 x 33.5 x 28.8 mm, 30 faces (baked)
FEATURE [App::Part] Top_7c43
  Group = -> [Shape,Shape001,Shape002]
  Origin = -> Origin003
FEATURE [App::Part] Step_Models_7c43
  Group = -> [Top_7c43]
  Origin = -> Origin002
FEATURE [App::Part] Board_7c43  label="power_supply"
  Group = -> [Local_CS_7c43,Board_Geoms_7c43,Step_Models_7c43]
  Origin = -> Origin001
PROVENANCE & LICENSES
A FreeCAD (.FCStd) document from a public repository crawl; recipes are the document's own serialized feature recipes (and, for linked parts, companion documents' recipes).
License: gpl-3.0.
